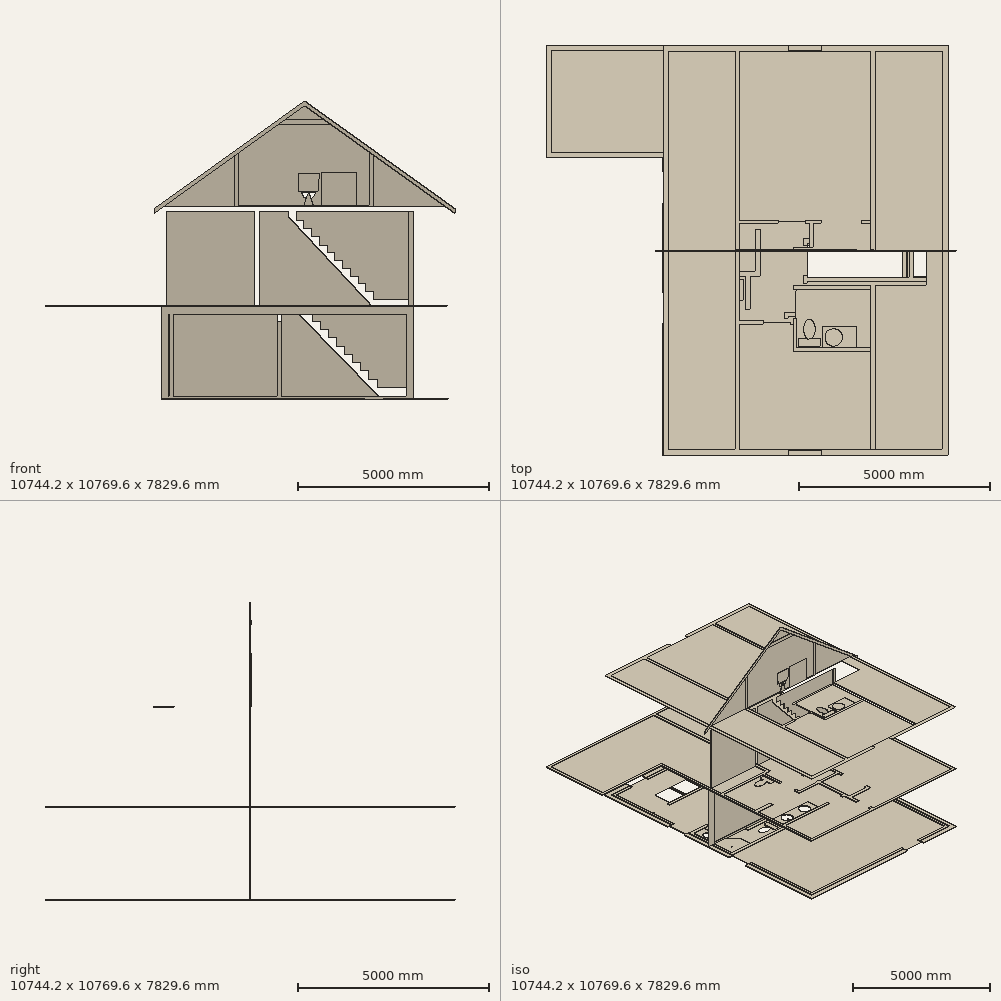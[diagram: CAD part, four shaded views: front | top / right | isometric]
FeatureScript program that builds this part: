
annotation { "Feature Type Name" : "Feature", "Feature Type Description" : "" }
export const myFeature = defineFeature(function(context is Context, id is Id, definition is map)
    precondition{}
    {
        {
            var Q0;
            Q0=qCreatedBy(makeId("Top.planeOp"),FACE);
            cPlane(context, id + "F0", {"entities" : qUnion([Q0]), "cplaneType" : CPlaneType.OFFSET, "offset" : 2438.4 * mm, "oppositeDirection" : true, "width" : 152.4 * mm, "height" : 152.4 * mm});
        }
        {
            var Q0;
            Q0=qCreatedBy(makeId("Top.planeOp"),FACE);
            cPlane(context, id + "F1", {"entities" : qUnion([Q0]), "cplaneType" : CPlaneType.OFFSET, "offset" : 2641.6 * mm, "width" : 152.4 * mm, "height" : 152.4 * mm});
        }
        {
            var Q0;
            Q0=qCreatedBy(id+"F0.planeOp",FACE);
            var sketch = newSketch(context, id + "F2", { "sketchPlane" : qUnion([Q0])});
            skLineSegment(sketch, "E0.bottom", {"start": v(-2901.95, -5207) * mm, "end": v(1898.65, -5207) * mm});
            skLineSegment(sketch, "E0.top", {"start": v(-2901.95, 5207) * mm, "end": v(3346.45, 5207) * mm});
            skLineSegment(sketch, "E0.left", {"start": v(-2901.95, -5207) * mm, "end": v(-2901.95, -1930.4) * mm});
            skLineSegment(sketch, "E0.right", {"start": v(4260.85, -5207) * mm, "end": v(4260.85, -863.6) * mm});
            skLineSegment(sketch, "E1.right", {"start": v(0, 5270.5) * mm, "end": v(0, -5207) * mm, "construction": true});
            skLineSegment(sketch, "E2", {"start": v(-2901.95, 0) * mm, "end": v(1722.7, 0) * mm, "construction": true});
            skLineSegment(sketch, "E3", {"start": v(463.55, -25.4) * mm, "end": v(463.55, -939.8) * mm});
            skLineSegment(sketch, "E4", {"start": v(463.55, -939.8) * mm, "end": v(666.75, -939.8) * mm});
            skLineSegment(sketch, "E5", {"start": v(666.75, -939.8) * mm, "end": v(666.75, -25.4) * mm});
            skLineSegment(sketch, "E6", {"start": v(666.75, -25.4) * mm, "end": v(869.95, -25.4) * mm});
            skLineSegment(sketch, "E7", {"start": v(869.95, -939.8) * mm, "end": v(869.95, -25.4) * mm});
            skLineSegment(sketch, "E8", {"start": v(463.55, -25.4) * mm, "end": v(666.75, -25.4) * mm});
            skLineSegment(sketch, "E9", {"start": v(666.75, -939.8) * mm, "end": v(869.95, -939.8) * mm});
            skLineSegment(sketch, "E10", {"start": v(869.95, -939.8) * mm, "end": v(1073.15, -939.8) * mm});
            skLineSegment(sketch, "E11", {"start": v(1073.15, -939.8) * mm, "end": v(1073.15, -25.4) * mm});
            skLineSegment(sketch, "E12", {"start": v(869.95, -25.4) * mm, "end": v(1073.15, -25.4) * mm});
            skLineSegment(sketch, "E13", {"start": v(1073.15, -25.4) * mm, "end": v(1276.35, -25.4) * mm});
            skLineSegment(sketch, "E14", {"start": v(1276.35, -939.8) * mm, "end": v(1276.35, -25.4) * mm});
            skLineSegment(sketch, "E15", {"start": v(1276.35, -939.8) * mm, "end": v(1073.15, -939.8) * mm});
            skLineSegment(sketch, "E16", {"start": v(1276.35, -25.4) * mm, "end": v(1479.55, -25.4) * mm});
            skLineSegment(sketch, "E17", {"start": v(1479.55, -25.4) * mm, "end": v(1479.55, -939.8) * mm});
            skLineSegment(sketch, "E18", {"start": v(1479.55, -939.8) * mm, "end": v(1276.35, -939.8) * mm});
            skLineSegment(sketch, "E19", {"start": v(1479.55, -25.4) * mm, "end": v(1682.75, -25.4) * mm});
            skLineSegment(sketch, "E20", {"start": v(1682.75, -25.4) * mm, "end": v(1682.75, -939.8) * mm});
            skLineSegment(sketch, "E21", {"start": v(1682.75, -939.8) * mm, "end": v(1479.55, -939.8) * mm});
            skLineSegment(sketch, "E22", {"start": v(1682.75, -25.4) * mm, "end": v(1885.95, -25.4) * mm});
            skLineSegment(sketch, "E23", {"start": v(1885.95, -25.4) * mm, "end": v(1885.95, -939.8) * mm});
            skLineSegment(sketch, "E24", {"start": v(1885.95, -939.8) * mm, "end": v(1682.75, -939.8) * mm});
            skLineSegment(sketch, "E25", {"start": v(1885.95, -25.4) * mm, "end": v(2089.15, -25.4) * mm});
            skLineSegment(sketch, "E26", {"start": v(2089.15, -25.4) * mm, "end": v(2089.15, -939.8) * mm});
            skLineSegment(sketch, "E27", {"start": v(2089.15, -939.8) * mm, "end": v(1885.95, -939.8) * mm});
            skLineSegment(sketch, "E28", {"start": v(2089.15, -25.4) * mm, "end": v(2292.35, -25.4) * mm});
            skLineSegment(sketch, "E29", {"start": v(2292.35, -25.4) * mm, "end": v(2292.35, -939.8) * mm});
            skLineSegment(sketch, "E30", {"start": v(2292.35, -939.8) * mm, "end": v(2089.15, -939.8) * mm});
            skLineSegment(sketch, "E31.bottom", {"start": v(-69.85, -1727.2) * mm, "end": v(69.85, -1727.2) * mm});
            skLineSegment(sketch, "E31.top", {"start": v(-69.85, -1879.6) * mm, "end": v(69.85, -1879.6) * mm});
            skLineSegment(sketch, "E31.left", {"start": v(-69.85, -1727.2) * mm, "end": v(-69.85, -1879.6) * mm});
            skLineSegment(sketch, "E31.right", {"start": v(69.85, -1727.2) * mm, "end": v(69.85, -1879.6) * mm});
            skLineSegment(sketch, "E32.bottom", {"start": v(69.85, 3175) * mm, "end": v(-69.85, 3175) * mm});
            skLineSegment(sketch, "E32.top", {"start": v(69.85, 3327.4) * mm, "end": v(-69.85, 3327.4) * mm});
            skLineSegment(sketch, "E32.left", {"start": v(69.85, 3175) * mm, "end": v(69.85, 3327.4) * mm});
            skLineSegment(sketch, "E32.right", {"start": v(-69.85, 3175) * mm, "end": v(-69.85, 3327.4) * mm});
            skLineSegment(sketch, "E33.0", {"start": v(4438.65, -5384.8) * mm, "end": v(4438.65, -685.8) * mm});
            skLineSegment(sketch, "E33.1", {"start": v(-3079.75, -5384.8) * mm, "end": v(4438.65, -5384.8) * mm});
            skLineSegment(sketch, "E33.2", {"start": v(-3079.75, -5384.8) * mm, "end": v(-3079.75, -1930.4) * mm});
            skLineSegment(sketch, "E33.3", {"start": v(-3079.75, 5384.8) * mm, "end": v(3524.25, 5384.8) * mm});
            skLineSegment(sketch, "E34", {"start": v(-3079.75, 2082.8) * mm, "end": v(-2901.95, 2082.8) * mm});
            skLineSegment(sketch, "E35", {"start": v(-3079.75, 1244.6) * mm, "end": v(-2901.95, 1244.6) * mm});
            skLineSegment(sketch, "E36", {"start": v(-2990.85, 2082.8) * mm, "end": v(-2482.7, 1416.2) * mm});
            skLineSegment(sketch, "E37", {"start": v(-2990.85, 2082.8) * mm, "end": v(-2990.85, 1244.6) * mm});
            skLineSegment(sketch, "E38", {"start": v(-2774.95, 1193.8) * mm, "end": v(-1962.15, 1193.8) * mm});
            skLineSegment(sketch, "E39", {"start": v(-2774.95, 1079.5) * mm, "end": v(-1962.15, 1079.5) * mm});
            skLineSegment(sketch, "E40", {"start": v(-2774.95, 1193.8) * mm, "end": v(-2774.95, 1079.5) * mm});
            skLineSegment(sketch, "E41", {"start": v(-1962.15, 1193.8) * mm, "end": v(-1962.15, 1079.5) * mm});
            skLineSegment(sketch, "E42", {"start": v(-1962.15, 1136.65) * mm, "end": v(-1250.95, 1136.65) * mm});
            skLineSegment(sketch, "E43", {"start": v(-1962.15, 1136.65) * mm, "end": v(-1324.41, 821.85) * mm});
            skLineSegment(sketch, "E44", {"start": v(-1250.95, 1193.8) * mm, "end": v(-1250.95, 1079.5) * mm});
            skLineSegment(sketch, "E45", {"start": v(-1250.95, 1193.8) * mm, "end": v(-768.35, 1193.8) * mm});
            skLineSegment(sketch, "E46", {"start": v(-1250.95, 1079.5) * mm, "end": v(-1149.35, 1079.5) * mm});
            skLineSegment(sketch, "E47", {"start": v(-1035.05, 1079.5) * mm, "end": v(-1035.05, -50.8) * mm});
            skLineSegment(sketch, "E48", {"start": v(-1149.35, 1079.5) * mm, "end": v(-1149.35, -165.1) * mm});
            skLineSegment(sketch, "E49", {"start": v(2241.55, -977.9) * mm, "end": v(-19.05, -977.9) * mm});
            skLineSegment(sketch, "E50", {"start": v(2241.55, -1066.8) * mm, "end": v(-19.05, -1066.8) * mm});
            skLineSegment(sketch, "E51.bottom", {"start": v(-251.05, -835.46) * mm, "end": v(-251.05, -276.66) * mm});
            skLineSegment(sketch, "E51.top", {"start": v(-454.25, -835.46) * mm, "end": v(-454.25, -276.66) * mm});
            skLineSegment(sketch, "E51.left", {"start": v(-454.25, -835.46) * mm, "end": v(-251.05, -835.46) * mm});
            skLineSegment(sketch, "E51.right", {"start": v(-454.25, -276.66) * mm, "end": v(-251.05, -276.66) * mm});
            skEllipse(sketch, "E52", {"center": v(-703.17, -556.06) * mm, "majorRadius": 259.08 * mm, "minorRadius": 152.4 * mm, "majorAxis": v(-1, 0)});
            skLineSegment(sketch, "E53", {"start": v(-454.25, -556.06) * mm, "end": v(-703.17, -556.06) * mm});
            skPoint(sketch, "E53.endSnap0", {"position": v(-962.25, -556.06) * mm});
            skLineSegment(sketch, "E54", {"start": v(206.15, -835.46) * mm, "end": v(-352.65, -835.46) * mm, "construction": true});
            skPoint(sketch, "E54.endSnap0", {"position": v(-352.65, -276.66) * mm});
            skLineSegment(sketch, "E55", {"start": v(-962.25, -556.06) * mm, "end": v(-330.86, -556.06) * mm});
            skLineSegment(sketch, "E56", {"start": v(-2876.55, -5181.6) * mm, "end": v(1898.65, -5181.6) * mm});
            skLineSegment(sketch, "E57", {"start": v(4235.45, -5181.6) * mm, "end": v(4235.45, -889) * mm});
            skLineSegment(sketch, "E58", {"start": v(4133.85, -990.6) * mm, "end": v(4133.85, -5080) * mm});
            skLineSegment(sketch, "E59", {"start": v(4133.85, -5080) * mm, "end": v(2736.85, -5080) * mm});
            skLineSegment(sketch, "E60", {"start": v(-2774.95, -5080) * mm, "end": v(-2774.95, -1930.4) * mm});
            skLineSegment(sketch, "E61", {"start": v(-2774.95, 1244.6) * mm, "end": v(-2876.55, 1244.6) * mm});
            skLineSegment(sketch, "E62", {"start": v(-2876.55, 1244.6) * mm, "end": v(-2876.55, -1092.2) * mm});
            skLineSegment(sketch, "E63", {"start": v(1898.65, -5080) * mm, "end": v(-2774.95, -5080) * mm});
            skLineSegment(sketch, "E64", {"start": v(4260.85, -863.6) * mm, "end": v(3346.45, -863.6) * mm});
            skLineSegment(sketch, "E65", {"start": v(3346.45, -863.6) * mm, "end": v(3346.45, 5207) * mm});
            skLineSegment(sketch, "E66", {"start": v(4438.65, -685.8) * mm, "end": v(3524.25, -685.8) * mm});
            skLineSegment(sketch, "E67", {"start": v(3524.25, -685.8) * mm, "end": v(3524.25, 5384.8) * mm});
            skLineSegment(sketch, "E68", {"start": v(3321.05, -889) * mm, "end": v(4235.45, -889) * mm});
            skLineSegment(sketch, "E69", {"start": v(4133.85, -990.6) * mm, "end": v(3219.45, -990.6) * mm});
            skLineSegment(sketch, "E70", {"start": v(3321.05, -889) * mm, "end": v(3321.05, 5181.6) * mm});
            skLineSegment(sketch, "E71", {"start": v(3219.45, -990.6) * mm, "end": v(3219.45, 5080) * mm});
            skLineSegment(sketch, "E72", {"start": v(3321.05, 5181.6) * mm, "end": v(-1098.55, 5181.6) * mm});
            skLineSegment(sketch, "E73", {"start": v(3219.45, 5080) * mm, "end": v(-1098.55, 5080) * mm});
            skLineSegment(sketch, "E74", {"start": v(-2876.55, 5181.6) * mm, "end": v(-2876.55, 2082.8) * mm});
            skLineSegment(sketch, "E75", {"start": v(-2774.95, 5080) * mm, "end": v(-2774.95, 2082.8) * mm});
            skLineSegment(sketch, "E76", {"start": v(-2876.55, 2082.8) * mm, "end": v(-2774.95, 2082.8) * mm});
            skLineSegment(sketch, "E77", {"start": v(-3079.75, -1092.2) * mm, "end": v(-2901.95, -1092.2) * mm});
            skLineSegment(sketch, "E78", {"start": v(-3079.75, -1930.4) * mm, "end": v(-2901.95, -1930.4) * mm});
            skLineSegment(sketch, "E79", {"start": v(-2990.85, -1092.2) * mm, "end": v(-2990.85, -1930.4) * mm});
            skLineSegment(sketch, "E80", {"start": v(-2876.55, -1092.2) * mm, "end": v(-2774.95, -1092.2) * mm});
            skLineSegment(sketch, "E81", {"start": v(-2876.55, -1930.4) * mm, "end": v(-2774.95, -1930.4) * mm});
            skLineSegment(sketch, "E82.trimOffspring", {"start": v(-2876.55, -1930.4) * mm, "end": v(-2876.55, -5181.6) * mm});
            skLineSegment(sketch, "E83.trimOffspring", {"start": v(-2774.95, -1092.2) * mm, "end": v(-2774.95, 1244.6) * mm});
            skLineSegment(sketch, "E84.trimOffspring", {"start": v(-2901.95, -1092.2) * mm, "end": v(-2901.95, 1244.6) * mm});
            skLineSegment(sketch, "E85.trimOffspring", {"start": v(-3079.75, -1092.2) * mm, "end": v(-3079.75, 1244.6) * mm});
            skLineSegment(sketch, "E86.trimOffspring", {"start": v(-3079.75, 2082.8) * mm, "end": v(-3079.75, 5384.8) * mm});
            skLineSegment(sketch, "E87.trimOffspring", {"start": v(-2901.95, 2082.8) * mm, "end": v(-2901.95, 5207) * mm});
            skLineSegment(sketch, "E88", {"start": v(-3079.75, -1092.2) * mm, "end": v(-3079.75, -1930.4) * mm});
            skLineSegment(sketch, "E89", {"start": v(-2901.95, -1092.2) * mm, "end": v(-2901.95, -1930.4) * mm});
            skLineSegment(sketch, "E90", {"start": v(-1936.75, 5384.8) * mm, "end": v(-1936.75, 5207) * mm});
            skLineSegment(sketch, "E91", {"start": v(-1098.55, 5384.8) * mm, "end": v(-1098.55, 5207) * mm});
            skLineSegment(sketch, "E92", {"start": v(-1936.75, 5295.9) * mm, "end": v(-1098.55, 5295.9) * mm});
            skLineSegment(sketch, "E93.trimOffspring", {"start": v(-1936.75, 5181.6) * mm, "end": v(-2876.55, 5181.6) * mm});
            skLineSegment(sketch, "E94.trimOffspring", {"start": v(-1936.75, 5080) * mm, "end": v(-2774.95, 5080) * mm});
            skLineSegment(sketch, "E95", {"start": v(-1936.75, 5181.6) * mm, "end": v(-1936.75, 5080) * mm});
            skLineSegment(sketch, "E96", {"start": v(-1098.55, 5181.6) * mm, "end": v(-1098.55, 5080) * mm});
            skLineSegment(sketch, "E97", {"start": v(-2774.95, -927.1) * mm, "end": v(-2774.95, -1066.8) * mm});
            skLineSegment(sketch, "E98", {"start": v(-2774.95, -927.1) * mm, "end": v(-133.35, -927.1) * mm});
            skLineSegment(sketch, "E99", {"start": v(-2774.95, -1066.8) * mm, "end": v(-19.05, -1066.8) * mm});
            skLineSegment(sketch, "E100.bottom", {"start": v(-1755.03, 3333.88) * mm, "end": v(-993.03, 3333.88) * mm});
            skLineSegment(sketch, "E100.top", {"start": v(-1755.03, 4095.88) * mm, "end": v(-993.03, 4095.88) * mm});
            skLineSegment(sketch, "E100.left", {"start": v(-1755.03, 3333.88) * mm, "end": v(-1755.03, 4095.88) * mm});
            skLineSegment(sketch, "E100.right", {"start": v(-993.03, 3333.88) * mm, "end": v(-993.03, 4095.88) * mm});
            skLineSegment(sketch, "E101.bottom", {"start": v(-908.34, 3329.81) * mm, "end": v(-146.34, 3329.81) * mm});
            skLineSegment(sketch, "E101.top", {"start": v(-908.34, 4091.81) * mm, "end": v(-146.34, 4091.81) * mm});
            skLineSegment(sketch, "E101.left", {"start": v(-908.34, 3329.81) * mm, "end": v(-908.34, 4091.81) * mm});
            skLineSegment(sketch, "E101.right", {"start": v(-146.34, 3329.81) * mm, "end": v(-146.34, 4091.81) * mm});
            skLineSegment(sketch, "E102.bottom", {"start": v(-2749.55, 139.7) * mm, "end": v(-2749.55, 1054.1) * mm});
            skLineSegment(sketch, "E102.top", {"start": v(-2216.15, 139.7) * mm, "end": v(-2216.15, 1054.1) * mm});
            skLineSegment(sketch, "E102.left", {"start": v(-2749.55, 139.7) * mm, "end": v(-2216.15, 139.7) * mm});
            skLineSegment(sketch, "E102.right", {"start": v(-2749.55, 1054.1) * mm, "end": v(-2216.15, 1054.1) * mm});
            skCircle(sketch, "E103", {"center": v(-2474.62, 596.9) * mm, "radius": 203.2 * mm});
            skLineSegment(sketch, "E104", {"start": v(-2474.62, 139.7) * mm, "end": v(-2474.62, 1054.1) * mm, "construction": true});
            skLineSegment(sketch, "E105", {"start": v(-1035.05, 1079.5) * mm, "end": v(-768.35, 1079.5) * mm});
            skLineSegment(sketch, "E106", {"start": v(-768.35, 1193.8) * mm, "end": v(-768.35, 1079.5) * mm});
            skLineSegment(sketch, "E107", {"start": v(-768.35, 1136.65) * mm, "end": v(-107.95, 1136.65) * mm});
            skLineSegment(sketch, "E108", {"start": v(-107.95, 1193.8) * mm, "end": v(-107.95, 1079.5) * mm});
            skLineSegment(sketch, "E109", {"start": v(-768.35, 1136.65) * mm, "end": v(-205.42, 1481.96) * mm});
            skLineSegment(sketch, "E110", {"start": v(-107.95, 1193.8) * mm, "end": v(298.45, 1193.8) * mm});
            skLineSegment(sketch, "E111", {"start": v(298.45, 1079.5) * mm, "end": v(298.45, 1193.8) * mm});
            skLineSegment(sketch, "E112", {"start": v(298.45, 1079.5) * mm, "end": v(-107.95, 1079.5) * mm});
            skLineSegment(sketch, "E113", {"start": v(1898.65, -5384.8) * mm, "end": v(1898.65, -5080) * mm});
            skLineSegment(sketch, "E114", {"start": v(2736.85, -5080) * mm, "end": v(2736.85, -5384.8) * mm});
            skLineSegment(sketch, "E115.trimOffspring", {"start": v(2736.85, -5181.6) * mm, "end": v(4235.45, -5181.6) * mm});
            skLineSegment(sketch, "E116.trimOffspring", {"start": v(2736.85, -5207) * mm, "end": v(4260.85, -5207) * mm});
            skLineSegment(sketch, "E117", {"start": v(1898.65, -5295.9) * mm, "end": v(2736.85, -5295.9) * mm});
            skLineSegment(sketch, "E118", {"start": v(2736.85, -5207) * mm, "end": v(2736.85, -5384.8) * mm});
            skLineSegment(sketch, "E119", {"start": v(1898.65, -5207) * mm, "end": v(1898.65, -5384.8) * mm});
            skLineSegment(sketch, "E120", {"start": v(184.15, 1079.5) * mm, "end": v(298.45, 1079.5) * mm});
            skLineSegment(sketch, "E121", {"start": v(298.45, 1079.5) * mm, "end": v(184.15, 1079.5) * mm});
            skLineSegment(sketch, "E122", {"start": v(184.15, 1079.5) * mm, "end": v(184.15, 12.7) * mm});
            skLineSegment(sketch, "E123", {"start": v(184.15, 12.7) * mm, "end": v(2241.55, 12.7) * mm});
            skLineSegment(sketch, "E124", {"start": v(2241.55, 12.7) * mm, "end": v(2241.55, 850.9) * mm});
            skLineSegment(sketch, "E125", {"start": v(1822.45, 850.9) * mm, "end": v(1822.45, 736.6) * mm});
            skLineSegment(sketch, "E126", {"start": v(1822.45, 736.6) * mm, "end": v(2127.25, 736.6) * mm});
            skLineSegment(sketch, "E127", {"start": v(2127.25, 736.6) * mm, "end": v(2127.25, 127) * mm});
            skLineSegment(sketch, "E128", {"start": v(2127.25, 127) * mm, "end": v(298.45, 127) * mm});
            skLineSegment(sketch, "E129", {"start": v(298.45, 127) * mm, "end": v(298.45, 1079.5) * mm});
            skLineSegment(sketch, "E130", {"start": v(-1149.35, -165.1) * mm, "end": v(-133.35, -165.1) * mm});
            skLineSegment(sketch, "E131", {"start": v(-133.35, -927.1) * mm, "end": v(-133.35, -165.1) * mm});
            skLineSegment(sketch, "E132", {"start": v(-1035.05, -50.8) * mm, "end": v(-19.05, -50.8) * mm});
            skLineSegment(sketch, "E133", {"start": v(-19.05, -50.8) * mm, "end": v(-19.05, -1066.8) * mm});
            skLineSegment(sketch, "E134", {"start": v(-19.05, -977.9) * mm, "end": v(-19.05, -1066.8) * mm});
            skLineSegment(sketch, "E135", {"start": v(-2770.45, -923.46) * mm, "end": v(-2770.45, 41.74) * mm});
            skLineSegment(sketch, "E136", {"start": v(-2770.45, 41.74) * mm, "end": v(-2262.45, 41.74) * mm});
            skLineSegment(sketch, "E137", {"start": v(-2262.45, 41.74) * mm, "end": v(-1803.35, -419.08) * mm});
            skLineSegment(sketch, "E138", {"start": v(-1803.35, -419.08) * mm, "end": v(-1805.26, -927.07) * mm});
            skLineSegment(sketch, "E139", {"start": v(-1805.26, -927.07) * mm, "end": v(-2770.45, -923.46) * mm});
            skLineSegment(sketch, "E140", {"start": v(-69.85, -927.1) * mm, "end": v(-69.85, -1079.5) * mm});
            skLineSegment(sketch, "E141", {"start": v(-69.85, -1079.5) * mm, "end": v(69.85, -1079.5) * mm});
            skLineSegment(sketch, "E142", {"start": v(69.85, -1079.5) * mm, "end": v(69.85, -927.1) * mm});
            skLineSegment(sketch, "E143", {"start": v(69.85, -927.1) * mm, "end": v(-69.85, -927.1) * mm});
            skLineSegment(sketch, "E144", {"start": v(-69.85, 1016) * mm, "end": v(69.85, 1016) * mm});
            skLineSegment(sketch, "E145", {"start": v(69.85, 1016) * mm, "end": v(69.85, 1168.4) * mm});
            skLineSegment(sketch, "E146", {"start": v(69.85, 1168.4) * mm, "end": v(-69.85, 1168.4) * mm});
            skLineSegment(sketch, "E147", {"start": v(-69.85, 1168.4) * mm, "end": v(-69.85, 1016) * mm});
            skLineSegment(sketch, "E148", {"start": v(3219.45, -25.4) * mm, "end": v(3219.45, -939.8) * mm});
            skLineSegment(sketch, "E149", {"start": v(3219.45, -939.8) * mm, "end": v(2495.55, -939.8) * mm});
            skLineSegment(sketch, "E150", {"start": v(2495.55, -939.8) * mm, "end": v(2495.55, -25.4) * mm});
            skLineSegment(sketch, "E151", {"start": v(2495.55, -25.4) * mm, "end": v(3219.45, -25.4) * mm});
            skLineSegment(sketch, "E152", {"start": v(2292.35, -25.4) * mm, "end": v(2495.55, -25.4) * mm});
            skLineSegment(sketch, "E153", {"start": v(2292.35, -939.8) * mm, "end": v(2495.55, -939.8) * mm});
            skLineSegment(sketch, "E154", {"start": v(-528.09, 989.03) * mm, "end": v(-70.89, 989.03) * mm});
            skLineSegment(sketch, "E155", {"start": v(-70.89, 989.03) * mm, "end": v(-70.89, 74.64) * mm});
            skLineSegment(sketch, "E156", {"start": v(-70.89, 74.64) * mm, "end": v(-533.4, 74.64) * mm});
            skLineSegment(sketch, "E157", {"start": v(-533.4, 74.64) * mm, "end": v(-528.09, 989.03) * mm});
            skLineSegment(sketch, "E158", {"start": v(2241.55, -977.9) * mm, "end": v(2241.55, -1066.8) * mm});
            skCircle(sketch, "E159", {"center": v(-2465.65, -619.8) * mm, "radius": 25.37 * mm});
            skLineSegment(sketch, "E160", {"start": v(-2774.95, 3289.3) * mm, "end": v(-2774.95, 3175) * mm});
            skLineSegment(sketch, "E161", {"start": v(-2774.95, 3175) * mm, "end": v(-2698.75, 3175) * mm});
            skLineSegment(sketch, "E162", {"start": v(-2698.75, 3175) * mm, "end": v(-2698.75, 3289.3) * mm});
            skLineSegment(sketch, "E163", {"start": v(-2698.75, 3289.3) * mm, "end": v(-2774.95, 3289.3) * mm});
            skLineSegment(sketch, "E164", {"start": v(-2698.75, 3232.15) * mm, "end": v(-1885.95, 3232.15) * mm});
            skLineSegment(sketch, "E165", {"start": v(-1885.95, 3289.3) * mm, "end": v(-1885.95, 3175) * mm});
            skLineSegment(sketch, "E166", {"start": v(-1885.95, 3175) * mm, "end": v(69.85, 3175) * mm});
            skLineSegment(sketch, "E167", {"start": v(-69.85, 5080) * mm, "end": v(-69.85, 3289.3) * mm});
            skLineSegment(sketch, "E168", {"start": v(-69.85, 3289.3) * mm, "end": v(-1885.95, 3289.3) * mm});
            skLineSegment(sketch, "E169", {"start": v(-69.85, 5080) * mm, "end": v(69.85, 5080) * mm});
            skLineSegment(sketch, "E170", {"start": v(69.85, 5080) * mm, "end": v(69.85, 3175) * mm});
            skLineSegment(sketch, "E171", {"start": v(-2698.75, 3232.15) * mm, "end": v(-1944.43, 3534.9) * mm});
            skLineSegment(sketch, "E172", {"start": v(298.45, 850.9) * mm, "end": v(298.45, 736.6) * mm});
            skLineSegment(sketch, "E173", {"start": v(298.45, 736.6) * mm, "end": v(603.25, 736.6) * mm});
            skLineSegment(sketch, "E174", {"start": v(603.25, 736.6) * mm, "end": v(603.25, 850.9) * mm});
            skLineSegment(sketch, "E175", {"start": v(603.25, 850.9) * mm, "end": v(298.45, 850.9) * mm});
            skLineSegment(sketch, "E176", {"start": v(1822.45, 850.9) * mm, "end": v(2241.55, 850.9) * mm});
            skCircle(sketch, "E177", {"center": v(264.69, -453.92) * mm, "radius": 228.6 * mm});
            skSolve(sketch);
        }
        {
            var Q0;
            Q0=qCreatedBy(id+"F1.planeOp",FACE);
            var sketch = newSketch(context, id + "F3", { "sketchPlane" : qUnion([Q0])});
            skLineSegment(sketch, "E178.bottom", {"start": v(-2914.65, -5219.7) * mm, "end": v(4273.55, -5219.7) * mm});
            skLineSegment(sketch, "E178.top", {"start": v(-2914.65, 5219.7) * mm, "end": v(4273.55, 5219.7) * mm});
            skLineSegment(sketch, "E178.left", {"start": v(-2914.65, -5219.7) * mm, "end": v(-2914.65, 5219.7) * mm});
            skLineSegment(sketch, "E178.right", {"start": v(4273.55, -5219.7) * mm, "end": v(4273.55, 5219.7) * mm});
            skLineSegment(sketch, "E179", {"start": v(-3657.6, 0) * mm, "end": v(4273.55, 0) * mm, "construction": true});
            skLineSegment(sketch, "E180", {"start": v(0, 5257.8) * mm, "end": v(0, -5257.8) * mm, "construction": true});
            skLineSegment(sketch, "E181.0", {"start": v(4425.95, -5372.1) * mm, "end": v(4425.95, 5372.1) * mm});
            skLineSegment(sketch, "E181.1", {"start": v(-3067.05, -5372.1) * mm, "end": v(4425.95, -5372.1) * mm});
            skLineSegment(sketch, "E181.2", {"start": v(-3067.05, -5372.1) * mm, "end": v(-3067.05, 5372.1) * mm});
            skLineSegment(sketch, "E181.3", {"start": v(-3067.05, 5372.1) * mm, "end": v(4425.95, 5372.1) * mm});
            skLineSegment(sketch, "E182", {"start": v(2381.25, 5219.7) * mm, "end": v(2381.25, -5219.7) * mm});
            skLineSegment(sketch, "E183", {"start": v(-1047.75, 5219.7) * mm, "end": v(-1047.75, -5219.7) * mm});
            skLineSegment(sketch, "E184.0", {"start": v(2508.25, 5219.7) * mm, "end": v(2508.25, -5219.7) * mm});
            skLineSegment(sketch, "E185.0", {"start": v(-1174.75, 5219.7) * mm, "end": v(-1174.75, -5219.7) * mm});
            skLineSegment(sketch, "E186.left", {"start": v(3079.75, -12.7) * mm, "end": v(3079.75, -927.1) * mm});
            skLineSegment(sketch, "E187", {"start": v(2851.15, -12.7) * mm, "end": v(2851.15, -927.1) * mm});
            skLineSegment(sketch, "E188", {"start": v(2622.55, -12.7) * mm, "end": v(2622.55, -927.1) * mm});
            skLineSegment(sketch, "E189", {"start": v(2393.95, -927.1) * mm, "end": v(2393.95, -12.7) * mm});
            skLineSegment(sketch, "E190", {"start": v(2393.95, -12.7) * mm, "end": v(2165.35, -12.7) * mm});
            skLineSegment(sketch, "E191", {"start": v(2165.35, -12.7) * mm, "end": v(2165.35, -927.1) * mm});
            skLineSegment(sketch, "E192", {"start": v(1936.75, -927.1) * mm, "end": v(1936.75, -12.7) * mm});
            skLineSegment(sketch, "E193", {"start": v(1936.75, -12.7) * mm, "end": v(1708.15, -12.7) * mm});
            skLineSegment(sketch, "E194", {"start": v(1708.15, -12.7) * mm, "end": v(1708.15, -927.1) * mm});
            skLineSegment(sketch, "E195", {"start": v(1479.55, -927.1) * mm, "end": v(1479.55, -12.7) * mm});
            skLineSegment(sketch, "E196", {"start": v(1479.55, -12.7) * mm, "end": v(1250.95, -12.7) * mm});
            skLineSegment(sketch, "E197", {"start": v(1250.95, -12.7) * mm, "end": v(1250.95, -927.1) * mm});
            skLineSegment(sketch, "E198", {"start": v(1022.35, -927.1) * mm, "end": v(1022.35, -12.7) * mm});
            skLineSegment(sketch, "E199", {"start": v(2851.15, -12.7) * mm, "end": v(3079.75, -12.7) * mm});
            skLineSegment(sketch, "E200", {"start": v(1022.35, -12.7) * mm, "end": v(793.75, -12.7) * mm});
            skLineSegment(sketch, "E201", {"start": v(793.75, -12.7) * mm, "end": v(793.75, -927.1) * mm});
            skLineSegment(sketch, "E202", {"start": v(565.15, -927.1) * mm, "end": v(565.15, -12.7) * mm});
            skLineSegment(sketch, "E203", {"start": v(565.15, -12.7) * mm, "end": v(336.55, -12.7) * mm});
            skLineSegment(sketch, "E204", {"start": v(336.55, -12.7) * mm, "end": v(336.55, -927.1) * mm});
            skLineSegment(sketch, "E205", {"start": v(1098.55, 5219.7) * mm, "end": v(1098.55, 5372.1) * mm});
            skLineSegment(sketch, "E206", {"start": v(234.95, 5219.7) * mm, "end": v(234.95, 5372.1) * mm});
            skLineSegment(sketch, "E207", {"start": v(1098.55, 5295.9) * mm, "end": v(234.95, 5295.9) * mm});
            skLineSegment(sketch, "E208", {"start": v(666.75, 4864.1) * mm, "end": v(666.75, 5295.9) * mm, "construction": true});
            skLineSegment(sketch, "E209", {"start": v(1098.55, -5219.7) * mm, "end": v(1098.55, -5372.1) * mm});
            skLineSegment(sketch, "E210", {"start": v(1098.55, -5372.1) * mm, "end": v(1098.55, -5295.9) * mm});
            skLineSegment(sketch, "E211", {"start": v(1098.55, -5295.9) * mm, "end": v(234.95, -5295.9) * mm});
            skLineSegment(sketch, "E212", {"start": v(234.95, -5219.7) * mm, "end": v(234.95, -5372.1) * mm});
            skLineSegment(sketch, "E213", {"start": v(666.75, -5295.9) * mm, "end": v(666.75, -5575.3) * mm, "construction": true});
            skLineSegment(sketch, "E214", {"start": v(-31.75, 800.1) * mm, "end": v(-31.75, 698.5) * mm});
            skLineSegment(sketch, "E215", {"start": v(679.45, 800.1) * mm, "end": v(679.45, 698.5) * mm});
            skLineSegment(sketch, "E216", {"start": v(-1047.75, 698.5) * mm, "end": v(-31.75, 698.5) * mm});
            skLineSegment(sketch, "E217", {"start": v(-1047.75, 800.1) * mm, "end": v(-31.75, 800.1) * mm});
            skLineSegment(sketch, "E218", {"start": v(3841.75, -12.7) * mm, "end": v(3079.75, -12.7) * mm});
            skLineSegment(sketch, "E219", {"start": v(3841.75, -927.1) * mm, "end": v(3079.75, -927.1) * mm});
            skLineSegment(sketch, "E220", {"start": v(565.15, -12.7) * mm, "end": v(793.75, -12.7) * mm});
            skLineSegment(sketch, "E221", {"start": v(1022.35, -12.7) * mm, "end": v(1250.95, -12.7) * mm});
            skLineSegment(sketch, "E222", {"start": v(1479.55, -12.7) * mm, "end": v(1708.15, -12.7) * mm});
            skLineSegment(sketch, "E223", {"start": v(1936.75, -12.7) * mm, "end": v(2165.35, -12.7) * mm});
            skLineSegment(sketch, "E224", {"start": v(2393.95, -12.7) * mm, "end": v(2622.55, -12.7) * mm});
            skLineSegment(sketch, "E225", {"start": v(2622.55, -12.7) * mm, "end": v(2851.15, -12.7) * mm});
            skLineSegment(sketch, "E226", {"start": v(3079.75, -927.1) * mm, "end": v(336.55, -927.1) * mm});
            skLineSegment(sketch, "E227", {"start": v(-31.75, 749.3) * mm, "end": v(679.45, 749.3) * mm});
            skLineSegment(sketch, "E228", {"start": v(42.68, 1066.05) * mm, "end": v(679.45, 749.3) * mm});
            skLineSegment(sketch, "E229", {"start": v(679.45, 800.1) * mm, "end": v(1085.85, 800.1) * mm});
            skLineSegment(sketch, "E230", {"start": v(1085.85, 800.1) * mm, "end": v(1085.85, 698.5) * mm});
            skLineSegment(sketch, "E231", {"start": v(882.65, 88.9) * mm, "end": v(781.05, 88.9) * mm});
            skLineSegment(sketch, "E232", {"start": v(781.05, 88.9) * mm, "end": v(781.05, 698.5) * mm});
            skLineSegment(sketch, "E233", {"start": v(1085.85, 698.5) * mm, "end": v(679.45, 698.5) * mm});
            skLineSegment(sketch, "E234", {"start": v(450.85, -2552.7) * mm, "end": v(2381.25, -2552.7) * mm});
            skLineSegment(sketch, "E235", {"start": v(450.85, -2552.7) * mm, "end": v(450.85, -2654.3) * mm});
            skLineSegment(sketch, "E236", {"start": v(2381.25, -2654.3) * mm, "end": v(450.85, -2654.3) * mm});
            skLineSegment(sketch, "E237.bottom", {"start": v(1111.25, -2006.6) * mm, "end": v(2025.65, -2006.6) * mm});
            skLineSegment(sketch, "E237.top", {"start": v(1111.25, -2540) * mm, "end": v(2025.65, -2540) * mm});
            skLineSegment(sketch, "E237.left", {"start": v(1111.25, -2006.6) * mm, "end": v(1111.25, -2540) * mm});
            skLineSegment(sketch, "E237.right", {"start": v(2025.65, -2006.6) * mm, "end": v(2025.65, -2540) * mm});
            skCircle(sketch, "E238", {"center": v(1416.05, -2286) * mm, "radius": 228.6 * mm});
            skLineSegment(sketch, "E239.bottom", {"start": v(349.25, -1028.7) * mm, "end": v(2381.25, -1028.7) * mm});
            skLineSegment(sketch, "E239.top", {"start": v(349.25, -927.1) * mm, "end": v(2381.25, -927.1) * mm});
            skLineSegment(sketch, "E239.right", {"start": v(2381.25, -927.1) * mm, "end": v(2381.25, -1028.7) * mm});
            skLineSegment(sketch, "E240", {"start": v(349.25, -927.1) * mm, "end": v(349.25, -1028.7) * mm});
            skLineSegment(sketch, "E241.bottom", {"start": v(501.65, -2527.3) * mm, "end": v(1060.45, -2527.3) * mm});
            skLineSegment(sketch, "E241.top", {"start": v(501.65, -2324.1) * mm, "end": v(1060.45, -2324.1) * mm});
            skLineSegment(sketch, "E241.left", {"start": v(501.65, -2324.1) * mm, "end": v(501.65, -2527.3) * mm});
            skLineSegment(sketch, "E241.right", {"start": v(1060.45, -2324.1) * mm, "end": v(1060.45, -2527.3) * mm});
            skEllipse(sketch, "E242", {"center": v(781.05, -2075.18) * mm, "majorRadius": 259.08 * mm, "minorRadius": 152.4 * mm, "majorAxis": v(0, 1)});
            skLineSegment(sketch, "E243", {"start": v(781.05, -2324.1) * mm, "end": v(781.05, -2075.18) * mm});
            skPoint(sketch, "E243.endSnap0", {"position": v(781.05, -1816.1) * mm});
            skLineSegment(sketch, "E244", {"start": v(1060.45, -2425.7) * mm, "end": v(501.65, -2425.7) * mm, "construction": true});
            skPoint(sketch, "E244.endSnap0", {"position": v(1060.45, -2425.7) * mm});
            skLineSegment(sketch, "E245", {"start": v(781.05, -1816.1) * mm, "end": v(781.05, -2334.26) * mm});
            skLineSegment(sketch, "E246", {"start": v(349.25, -12.7) * mm, "end": v(2381.25, -12.7) * mm});
            skLineSegment(sketch, "E247", {"start": v(349.25, -12.7) * mm, "end": v(349.25, 88.9) * mm});
            skLineSegment(sketch, "E248", {"start": v(2381.25, 698.5) * mm, "end": v(2381.25, 800.1) * mm});
            skLineSegment(sketch, "E249", {"start": v(2381.25, 800.1) * mm, "end": v(2152.65, 800.1) * mm});
            skLineSegment(sketch, "E250", {"start": v(2152.65, 800.1) * mm, "end": v(2152.65, 698.5) * mm});
            skLineSegment(sketch, "E251", {"start": v(2152.65, 698.5) * mm, "end": v(2381.25, 698.5) * mm});
            skLineSegment(sketch, "E252", {"start": v(2381.25, -12.7) * mm, "end": v(2381.25, 88.9) * mm});
            skLineSegment(sketch, "E253", {"start": v(2381.25, 88.9) * mm, "end": v(349.25, 88.9) * mm});
            skLineSegment(sketch, "E254", {"start": v(781.05, 698.5) * mm, "end": v(882.65, 698.5) * mm});
            skLineSegment(sketch, "E255", {"start": v(882.65, 698.5) * mm, "end": v(882.65, 88.9) * mm});
            skLineSegment(sketch, "E256", {"start": v(349.25, -1028.7) * mm, "end": v(450.85, -1028.7) * mm});
            skLineSegment(sketch, "E257", {"start": v(450.85, -1028.7) * mm, "end": v(450.85, -1079.5) * mm});
            skLineSegment(sketch, "E258", {"start": v(450.85, -1079.5) * mm, "end": v(349.25, -1079.5) * mm});
            skLineSegment(sketch, "E259", {"start": v(349.25, -1079.5) * mm, "end": v(349.25, -1028.7) * mm});
            skLineSegment(sketch, "E260", {"start": v(400.05, -1079.5) * mm, "end": v(400.05, -1790.7) * mm});
            skLineSegment(sketch, "E261", {"start": v(400.05, -1079.5) * mm, "end": v(650.16, -1745.27) * mm});
            skLineSegment(sketch, "E262", {"start": v(349.25, -1790.7) * mm, "end": v(450.85, -1790.7) * mm});
            skLineSegment(sketch, "E263", {"start": v(450.85, -1790.7) * mm, "end": v(450.85, -2654.3) * mm});
            skLineSegment(sketch, "E264", {"start": v(450.85, -2654.3) * mm, "end": v(349.25, -2654.3) * mm});
            skLineSegment(sketch, "E265", {"start": v(349.25, -2654.3) * mm, "end": v(349.25, -1790.7) * mm});
            skLineSegment(sketch, "E266", {"start": v(349.25, -1829.9) * mm, "end": v(349.25, -1931.5) * mm});
            skLineSegment(sketch, "E267", {"start": v(349.25, -1931.5) * mm, "end": v(273.05, -1931.5) * mm});
            skLineSegment(sketch, "E268", {"start": v(273.05, -1931.5) * mm, "end": v(273.05, -1829.9) * mm});
            skLineSegment(sketch, "E269", {"start": v(273.05, -1829.9) * mm, "end": v(349.25, -1829.9) * mm});
            skLineSegment(sketch, "E270", {"start": v(273.05, -1880.7) * mm, "end": v(-438.15, -1880.7) * mm});
            skPoint(sketch, "E270.endSnap0", {"position": v(273.05, -1880.7) * mm});
            skLineSegment(sketch, "E271", {"start": v(-438.15, -1829.9) * mm, "end": v(-438.15, -1931.5) * mm});
            skLineSegment(sketch, "E272", {"start": v(273.05, -1880.7) * mm, "end": v(-313.04, -2283.57) * mm});
            skLineSegment(sketch, "E273", {"start": v(-438.15, -1829.9) * mm, "end": v(-1047.75, -1829.9) * mm});
            skLineSegment(sketch, "E274", {"start": v(-1047.75, -1829.9) * mm, "end": v(-1047.75, -1931.5) * mm});
            skLineSegment(sketch, "E275", {"start": v(-1047.75, -1931.5) * mm, "end": v(-438.15, -1931.5) * mm});
            skLineSegment(sketch, "E276", {"start": v(-1174.75, 5219.7) * mm, "end": v(-1047.75, 5219.7) * mm});
            skLineSegment(sketch, "E277", {"start": v(2508.25, 5219.7) * mm, "end": v(2381.25, 5219.7) * mm});
            skLineSegment(sketch, "E278", {"start": v(3841.75, -12.7) * mm, "end": v(3841.75, -927.1) * mm});
            skSolve(sketch);
        }
        {
            var Q0;
            Q0=qCreatedBy(makeId("Top.planeOp"),FACE);
            var sketch = newSketch(context, id + "F4", { "sketchPlane" : qUnion([Q0])});
            skLineSegment(sketch, "E279", {"start": v(-6115.05, 5372.1) * mm, "end": v(3511.55, 5372.1) * mm});
            skLineSegment(sketch, "E280", {"start": v(3511.55, 5372.1) * mm, "end": v(3511.55, 4660.9) * mm});
            skLineSegment(sketch, "E281", {"start": v(3511.55, 4660.9) * mm, "end": v(3892.55, 4660.9) * mm});
            skLineSegment(sketch, "E282", {"start": v(3892.55, 4660.9) * mm, "end": v(3892.55, 2197.1) * mm});
            skLineSegment(sketch, "E283", {"start": v(3892.55, 2197.1) * mm, "end": v(3511.55, 2197.1) * mm});
            skLineSegment(sketch, "E284", {"start": v(3511.55, 2197.1) * mm, "end": v(3511.55, -698.5) * mm});
            skLineSegment(sketch, "E285", {"start": v(3511.55, -698.5) * mm, "end": v(4425.95, -698.5) * mm});
            skLineSegment(sketch, "E286", {"start": v(4425.95, -698.5) * mm, "end": v(4425.95, -5372.1) * mm});
            skLineSegment(sketch, "E287", {"start": v(4425.95, -5372.1) * mm, "end": v(-3067.05, -5372.1) * mm});
            skLineSegment(sketch, "E288", {"start": v(-3067.05, -5372.1) * mm, "end": v(-3067.05, 2451.1) * mm});
            skLineSegment(sketch, "E289", {"start": v(-3067.05, 2451.1) * mm, "end": v(-6115.05, 2451.1) * mm});
            skLineSegment(sketch, "E290", {"start": v(-6115.05, 2451.1) * mm, "end": v(-6115.05, 5372.1) * mm});
            skLineSegment(sketch, "E291", {"start": v(-628.65, 5257.8) * mm, "end": v(-628.65, 1333.5) * mm});
            skLineSegment(sketch, "E292", {"start": v(-628.65, 1333.5) * mm, "end": v(-514.35, 1333.5) * mm});
            skLineSegment(sketch, "E293", {"start": v(-514.35, 1333.5) * mm, "end": v(-514.35, 5257.8) * mm});
            skLineSegment(sketch, "E294", {"start": v(-628.65, 5257.8) * mm, "end": v(-6000.75, 5257.8) * mm});
            skLineSegment(sketch, "E295", {"start": v(-6000.75, 5257.8) * mm, "end": v(-6000.75, 2565.4) * mm});
            skLineSegment(sketch, "E296", {"start": v(-6000.75, 2565.4) * mm, "end": v(-2952.75, 2565.4) * mm});
            skLineSegment(sketch, "E297", {"start": v(-2952.75, 2565.4) * mm, "end": v(-2952.75, -558.8) * mm});
            skLineSegment(sketch, "E298", {"start": v(-2952.75, -558.8) * mm, "end": v(-628.65, -558.8) * mm});
            skLineSegment(sketch, "E299", {"start": v(-628.65, -558.8) * mm, "end": v(-628.65, 558.8) * mm});
            skLineSegment(sketch, "E300", {"start": v(-628.65, 558.8) * mm, "end": v(-514.35, 558.8) * mm});
            skLineSegment(sketch, "E301", {"start": v(-514.35, 558.8) * mm, "end": v(-514.35, -673.1) * mm});
            skLineSegment(sketch, "E302", {"start": v(-514.35, -673.1) * mm, "end": v(-781.05, -673.1) * mm});
            skLineSegment(sketch, "E303", {"start": v(-781.05, -673.1) * mm, "end": v(-781.05, -1562.1) * mm});
            skLineSegment(sketch, "E304", {"start": v(-781.05, -2451.1) * mm, "end": v(120.65, -2451.1) * mm});
            skLineSegment(sketch, "E305", {"start": v(120.65, -2565.4) * mm, "end": v(-895.35, -2565.4) * mm});
            skLineSegment(sketch, "E306", {"start": v(-895.35, -1562.1) * mm, "end": v(-895.35, -673.1) * mm});
            skLineSegment(sketch, "E307", {"start": v(-895.35, -673.1) * mm, "end": v(-2952.75, -673.1) * mm});
            skLineSegment(sketch, "E308", {"start": v(-2952.75, -673.1) * mm, "end": v(-2952.75, -2324.1) * mm});
            skLineSegment(sketch, "E309", {"start": v(-2952.75, -2324.1) * mm, "end": v(-2190.75, -2324.1) * mm});
            skLineSegment(sketch, "E310", {"start": v(-2190.75, -2324.1) * mm, "end": v(-2190.75, -2476.5) * mm});
            skLineSegment(sketch, "E311", {"start": v(-2190.75, -2476.5) * mm, "end": v(-2952.75, -2476.5) * mm});
            skLineSegment(sketch, "E312", {"start": v(-2952.75, -2476.5) * mm, "end": v(-2952.75, -3771.9) * mm});
            skLineSegment(sketch, "E313", {"start": v(-2952.75, -3771.9) * mm, "end": v(-666.75, -3771.9) * mm});
            skLineSegment(sketch, "E314", {"start": v(120.65, -3771.9) * mm, "end": v(120.65, -2565.4) * mm});
            skLineSegment(sketch, "E315", {"start": v(120.65, -2451.1) * mm, "end": v(120.65, -2400.3) * mm});
            skLineSegment(sketch, "E316", {"start": v(120.65, -2400.3) * mm, "end": v(234.95, -2400.3) * mm});
            skLineSegment(sketch, "E317", {"start": v(234.95, -2400.3) * mm, "end": v(234.95, -2451.1) * mm});
            skLineSegment(sketch, "E318", {"start": v(234.95, -2451.1) * mm, "end": v(1123.95, -2451.1) * mm});
            skLineSegment(sketch, "E319", {"start": v(1123.95, -2451.1) * mm, "end": v(1123.95, -1739.9) * mm});
            skLineSegment(sketch, "E320", {"start": v(1123.95, -1739.9) * mm, "end": v(234.95, -1739.9) * mm});
            skLineSegment(sketch, "E321", {"start": v(234.95, -1739.9) * mm, "end": v(234.95, -1790.7) * mm});
            skLineSegment(sketch, "E322", {"start": v(234.95, -1790.7) * mm, "end": v(120.65, -1790.7) * mm});
            skLineSegment(sketch, "E323", {"start": v(120.65, -1790.7) * mm, "end": v(120.65, -1625.6) * mm});
            skLineSegment(sketch, "E324", {"start": v(120.65, -1625.6) * mm, "end": v(610.92, -1625.6) * mm});
            skLineSegment(sketch, "E325", {"start": v(610.92, -1625.6) * mm, "end": v(610.92, -1574.8) * mm});
            skLineSegment(sketch, "E326", {"start": v(610.92, -1574.8) * mm, "end": v(725.22, -1574.8) * mm});
            skLineSegment(sketch, "E327", {"start": v(725.22, -1574.8) * mm, "end": v(725.22, -1625.6) * mm});
            skLineSegment(sketch, "E328", {"start": v(725.22, -1625.6) * mm, "end": v(1238.25, -1625.6) * mm});
            skLineSegment(sketch, "E329", {"start": v(1238.25, -1625.6) * mm, "end": v(1238.25, -2717.8) * mm});
            skLineSegment(sketch, "E330", {"start": v(1238.25, -2717.8) * mm, "end": v(1123.95, -2717.8) * mm});
            skLineSegment(sketch, "E331", {"start": v(1123.95, -2717.8) * mm, "end": v(1123.95, -2565.4) * mm});
            skLineSegment(sketch, "E332", {"start": v(1123.95, -2565.4) * mm, "end": v(234.95, -2565.4) * mm});
            skLineSegment(sketch, "E333", {"start": v(234.95, -2565.4) * mm, "end": v(234.95, -4025.9) * mm});
            skLineSegment(sketch, "E334", {"start": v(234.95, -4025.9) * mm, "end": v(1123.95, -4025.9) * mm});
            skLineSegment(sketch, "E335", {"start": v(1123.95, -4025.9) * mm, "end": v(1123.95, -3937) * mm});
            skLineSegment(sketch, "E336", {"start": v(1123.95, -3937) * mm, "end": v(1238.25, -3937) * mm});
            skLineSegment(sketch, "E337", {"start": v(1238.25, -3937) * mm, "end": v(1238.25, -4140.2) * mm});
            skLineSegment(sketch, "E338", {"start": v(1238.25, -4140.2) * mm, "end": v(234.95, -4140.2) * mm});
            skLineSegment(sketch, "E339", {"start": v(234.95, -4140.2) * mm, "end": v(234.95, -4521.2) * mm});
            skLineSegment(sketch, "E340", {"start": v(234.95, -4521.2) * mm, "end": v(120.65, -4521.2) * mm});
            skLineSegment(sketch, "E341", {"start": v(120.65, -4521.2) * mm, "end": v(120.65, -3886.2) * mm});
            skLineSegment(sketch, "E342", {"start": v(-666.75, -3886.2) * mm, "end": v(-2952.75, -3886.2) * mm});
            skLineSegment(sketch, "E343", {"start": v(-2952.75, -3886.2) * mm, "end": v(-2952.75, -5257.8) * mm});
            skLineSegment(sketch, "E344", {"start": v(-2952.75, -5257.8) * mm, "end": v(120.65, -5257.8) * mm});
            skLineSegment(sketch, "E345", {"start": v(120.65, -5257.8) * mm, "end": v(120.65, -5130.8) * mm});
            skLineSegment(sketch, "E346", {"start": v(120.65, -5130.8) * mm, "end": v(234.95, -5130.8) * mm});
            skLineSegment(sketch, "E347", {"start": v(234.95, -5130.8) * mm, "end": v(234.95, -5257.8) * mm});
            skLineSegment(sketch, "E348", {"start": v(234.95, -5257.8) * mm, "end": v(4311.65, -5257.8) * mm});
            skLineSegment(sketch, "E349", {"start": v(4311.65, -5257.8) * mm, "end": v(4311.65, -812.8) * mm});
            skLineSegment(sketch, "E350", {"start": v(4311.65, -812.8) * mm, "end": v(725.22, -812.8) * mm});
            skLineSegment(sketch, "E351", {"start": v(725.22, -812.8) * mm, "end": v(725.22, -863.6) * mm});
            skLineSegment(sketch, "E352", {"start": v(725.22, -863.6) * mm, "end": v(610.92, -863.6) * mm});
            skLineSegment(sketch, "E353", {"start": v(610.92, -863.6) * mm, "end": v(610.92, -647.7) * mm});
            skLineSegment(sketch, "E354", {"start": v(610.92, -647.7) * mm, "end": v(725.22, -647.7) * mm});
            skLineSegment(sketch, "E355", {"start": v(725.22, -647.7) * mm, "end": v(725.22, -698.5) * mm});
            skLineSegment(sketch, "E356", {"start": v(725.22, -698.5) * mm, "end": v(3397.25, -698.5) * mm});
            skLineSegment(sketch, "E357", {"start": v(3397.25, -698.5) * mm, "end": v(3397.25, 190.5) * mm});
            skLineSegment(sketch, "E358", {"start": v(2584.45, 190.5) * mm, "end": v(725.22, 190.5) * mm});
            skLineSegment(sketch, "E359", {"start": v(725.22, 190.5) * mm, "end": v(725.22, 139.7) * mm});
            skLineSegment(sketch, "E360", {"start": v(725.22, 139.7) * mm, "end": v(610.92, 139.7) * mm});
            skLineSegment(sketch, "E361", {"start": v(610.92, 139.7) * mm, "end": v(610.92, 304.8) * mm});
            skLineSegment(sketch, "E362", {"start": v(610.92, 304.8) * mm, "end": v(2584.45, 304.8) * mm});
            skLineSegment(sketch, "E363", {"start": v(3397.25, 304.8) * mm, "end": v(3397.25, 2311.4) * mm});
            skLineSegment(sketch, "E364", {"start": v(3397.25, 2311.4) * mm, "end": v(3778.25, 2311.4) * mm});
            skLineSegment(sketch, "E365", {"start": v(3778.25, 2311.4) * mm, "end": v(3778.25, 4546.6) * mm});
            skLineSegment(sketch, "E366", {"start": v(3778.25, 4546.6) * mm, "end": v(3397.25, 4546.6) * mm});
            skLineSegment(sketch, "E367", {"start": v(3397.25, 4546.6) * mm, "end": v(3397.25, 5257.8) * mm});
            skLineSegment(sketch, "E368", {"start": v(3397.25, 5257.8) * mm, "end": v(-514.35, 5257.8) * mm});
            skLineSegment(sketch, "E369.bottom", {"start": v(-2947.9, -3233.86) * mm, "end": v(-2033.5, -3233.86) * mm});
            skLineSegment(sketch, "E369.top", {"start": v(-2947.9, -3767.26) * mm, "end": v(-2033.5, -3767.26) * mm});
            skLineSegment(sketch, "E369.left", {"start": v(-2947.9, -3233.86) * mm, "end": v(-2947.9, -3767.26) * mm});
            skLineSegment(sketch, "E369.right", {"start": v(-2033.5, -3233.86) * mm, "end": v(-2033.5, -3767.26) * mm});
            skCircle(sketch, "E370", {"center": v(-2490.7, -3513.26) * mm, "radius": 228.6 * mm});
            skLineSegment(sketch, "E371.bottom", {"start": v(-951.03, -1326.1) * mm, "end": v(-951.03, -767.3) * mm});
            skLineSegment(sketch, "E371.top", {"start": v(-1154.23, -1326.1) * mm, "end": v(-1154.23, -767.3) * mm});
            skLineSegment(sketch, "E371.left", {"start": v(-1154.23, -1326.1) * mm, "end": v(-951.03, -1326.1) * mm});
            skLineSegment(sketch, "E371.right", {"start": v(-1154.23, -767.3) * mm, "end": v(-951.03, -767.3) * mm});
            skEllipse(sketch, "E372", {"center": v(-1403.15, -1046.7) * mm, "majorRadius": 259.08 * mm, "minorRadius": 152.4 * mm, "majorAxis": v(-1, 0)});
            skLineSegment(sketch, "E373", {"start": v(-1154.23, -1046.7) * mm, "end": v(-1403.15, -1046.7) * mm});
            skPoint(sketch, "E373.endSnap0", {"position": v(-1662.23, -1046.7) * mm});
            skLineSegment(sketch, "E374", {"start": v(-493.83, -1326.1) * mm, "end": v(-1052.63, -1326.1) * mm, "construction": true});
            skPoint(sketch, "E374.endSnap0", {"position": v(-1052.63, -767.3) * mm});
            skLineSegment(sketch, "E375", {"start": v(-1662.23, -1046.7) * mm, "end": v(-1154.23, -1046.7) * mm});
            skLineSegment(sketch, "E376.bottom", {"start": v(-2033.5, -3233.86) * mm, "end": v(-1119.1, -3233.86) * mm});
            skLineSegment(sketch, "E376.top", {"start": v(-2033.5, -3767.26) * mm, "end": v(-1119.1, -3767.26) * mm});
            skLineSegment(sketch, "E376.right", {"start": v(-1119.1, -3233.86) * mm, "end": v(-1119.1, -3767.26) * mm});
            skCircle(sketch, "E377", {"center": v(-1576.3, -3513.26) * mm, "radius": 228.6 * mm});
            skLineSegment(sketch, "E378.bottom", {"start": v(-2851.15, -2857.5) * mm, "end": v(-2749.55, -2857.5) * mm});
            skLineSegment(sketch, "E378.top", {"start": v(-2851.15, -3111.5) * mm, "end": v(-2749.55, -3111.5) * mm});
            skLineSegment(sketch, "E378.left", {"start": v(-2851.15, -2857.5) * mm, "end": v(-2851.15, -3111.5) * mm});
            skLineSegment(sketch, "E378.right", {"start": v(-2749.55, -2857.5) * mm, "end": v(-2749.55, -3111.5) * mm});
            skLineSegment(sketch, "E379", {"start": v(-666.75, -3886.2) * mm, "end": v(-666.75, -3771.9) * mm});
            skLineSegment(sketch, "E380", {"start": v(120.65, -3771.9) * mm, "end": v(44.45, -3771.9) * mm});
            skLineSegment(sketch, "E381", {"start": v(44.45, -3771.9) * mm, "end": v(44.45, -3886.2) * mm});
            skLineSegment(sketch, "E382", {"start": v(44.45, -3886.2) * mm, "end": v(120.65, -3886.2) * mm});
            skLineSegment(sketch, "E383", {"start": v(3397.25, 304.8) * mm, "end": v(3295.65, 304.8) * mm});
            skLineSegment(sketch, "E384", {"start": v(3295.65, 304.8) * mm, "end": v(3295.65, 190.5) * mm});
            skLineSegment(sketch, "E385", {"start": v(3295.65, 190.5) * mm, "end": v(3397.25, 190.5) * mm});
            skLineSegment(sketch, "E386", {"start": v(2584.45, 304.8) * mm, "end": v(2584.45, 190.5) * mm});
            skLineSegment(sketch, "E387", {"start": v(2584.45, 190.5) * mm, "end": v(3295.65, 190.5) * mm});
            skLineSegment(sketch, "E388", {"start": v(725.22, -647.7) * mm, "end": v(725.22, 139.7) * mm});
            skLineSegment(sketch, "E389", {"start": v(-895.35, -1562.1) * mm, "end": v(-781.05, -1562.1) * mm});
            skLineSegment(sketch, "E390", {"start": v(-895.35, -2273.3) * mm, "end": v(-781.05, -2273.3) * mm});
            skLineSegment(sketch, "E391", {"start": v(-781.05, -2273.3) * mm, "end": v(-781.05, -2451.1) * mm});
            skLineSegment(sketch, "E392", {"start": v(-895.35, -2273.3) * mm, "end": v(-895.35, -2565.4) * mm});
            skSolve(sketch);
        }
        {
            var Q0;
            Q0=qCreatedBy(makeId("Front.planeOp"),FACE);
            var sketch = newSketch(context, id + "F5", { "sketchPlane" : qUnion([Q0])});
            skLineSegment(sketch, "E393", {"start": v(2381.25, 2641.6) * mm, "end": v(2381.25, 3962.4) * mm});
            skLineSegment(sketch, "E394", {"start": v(-1047.75, 2641.6) * mm, "end": v(2381.25, 2641.6) * mm});
            skLineSegment(sketch, "E395", {"start": v(781.05, 2641.6) * mm, "end": v(781.05, 3022.6) * mm});
            skLineSegment(sketch, "E396", {"start": v(527.05, 3022.6) * mm, "end": v(1035.05, 3022.6) * mm});
            skLineSegment(sketch, "E397", {"start": v(1035.05, 3022.6) * mm, "end": v(1060.45, 3479.8) * mm});
            skLineSegment(sketch, "E398", {"start": v(1060.45, 3479.8) * mm, "end": v(501.65, 3479.8) * mm});
            skLineSegment(sketch, "E399", {"start": v(501.65, 3479.8) * mm, "end": v(527.05, 3022.6) * mm});
            skLineSegment(sketch, "E400", {"start": v(603.25, 2997.2) * mm, "end": v(958.85, 2997.2) * mm});
            skArc(sketch, "E401", {"start": v(603.25, 2997.2) * mm, "mid": v(781.05, 2819.4) * mm, "end": v(958.85, 2997.2) * mm});
            skLineSegment(sketch, "E402", {"start": v(654.05, 2641.6) * mm, "end": v(908.05, 2641.6) * mm});
            skLineSegment(sketch, "E403", {"start": v(908.05, 2641.6) * mm, "end": v(781.05, 2997.2) * mm});
            skLineSegment(sketch, "E404", {"start": v(781.05, 2997.2) * mm, "end": v(654.05, 2641.6) * mm});
            skPoint(sketch, "E405", {"position": v(781.05, 3479.8) * mm});
            skLineSegment(sketch, "E406", {"start": v(1111.25, 3505.2) * mm, "end": v(2025.65, 3505.2) * mm});
            skLineSegment(sketch, "E407", {"start": v(2025.65, 3505.2) * mm, "end": v(2025.65, 2641.6) * mm});
            skLineSegment(sketch, "E408", {"start": v(2025.65, 2641.6) * mm, "end": v(1111.25, 2641.6) * mm});
            skLineSegment(sketch, "E409", {"start": v(1111.25, 2641.6) * mm, "end": v(1111.25, 3505.2) * mm});
            skLineSegment(sketch, "E410", {"start": v(3397.25, 2482.85) * mm, "end": v(3524.25, 2482.85) * mm});
            skLineSegment(sketch, "E411", {"start": v(3524.25, 2482.85) * mm, "end": v(3524.25, 0) * mm});
            skLineSegment(sketch, "E412", {"start": v(3397.25, 0) * mm, "end": v(3397.25, 2482.85) * mm});
            skLineSegment(sketch, "E413", {"start": v(3397.25, 0) * mm, "end": v(3524.25, 0) * mm});
            skLineSegment(sketch, "E414", {"start": v(3346.45, -209.55) * mm, "end": v(3524.25, -209.55) * mm});
            skLineSegment(sketch, "E415", {"start": v(3524.25, -209.55) * mm, "end": v(3524.25, -2343.15) * mm});
            skLineSegment(sketch, "E416", {"start": v(3524.25, -2343.15) * mm, "end": v(3346.45, -2343.15) * mm});
            skLineSegment(sketch, "E417", {"start": v(3346.45, -2343.15) * mm, "end": v(3346.45, -209.55) * mm});
            skLineSegment(sketch, "E418", {"start": v(2381.25, 2641.6) * mm, "end": v(2381.25, 2622.55) * mm});
            skLineSegment(sketch, "E419", {"start": v(2381.25, 2622.55) * mm, "end": v(-1047.75, 2622.55) * mm});
            skLineSegment(sketch, "E420", {"start": v(-1047.75, 2641.6) * mm, "end": v(-1047.75, 2622.55) * mm});
            skLineSegment(sketch, "E421", {"start": v(2381.25, 2622.55) * mm, "end": v(2470.15, 2622.55) * mm});
            skLineSegment(sketch, "E422", {"start": v(2470.15, 2622.55) * mm, "end": v(2470.15, 3976.9) * mm});
            skLineSegment(sketch, "E423", {"start": v(2470.15, 3976.9) * mm, "end": v(2381.25, 4040.58) * mm});
            skLineSegment(sketch, "E424", {"start": v(2381.25, 4040.58) * mm, "end": v(2381.25, 2622.55) * mm});
            skLineSegment(sketch, "E425", {"start": v(4425.95, 2622.55) * mm, "end": v(4425.95, 2482.85) * mm});
            skLineSegment(sketch, "E426", {"start": v(4425.95, 2482.85) * mm, "end": v(-3067.05, 2482.85) * mm});
            skLineSegment(sketch, "E427", {"start": v(-3067.05, 2482.85) * mm, "end": v(-3067.05, 2622.55) * mm});
            skLineSegment(sketch, "E428", {"start": v(-3067.05, 2622.55) * mm, "end": v(4425.95, 2622.55) * mm});
            skLineSegment(sketch, "E429", {"start": v(-3067.05, 2482.85) * mm, "end": v(-2940.3, 2482.85) * mm});
            skLineSegment(sketch, "E430", {"start": v(-2940.3, 2482.85) * mm, "end": v(-2940.3, 0) * mm});
            skLineSegment(sketch, "E431", {"start": v(-2940.3, 0) * mm, "end": v(-3067.05, 0) * mm});
            skLineSegment(sketch, "E432", {"start": v(-3067.05, 0) * mm, "end": v(-3067.05, 2482.85) * mm});
            skLineSegment(sketch, "E433", {"start": v(-628.65, 2482.85) * mm, "end": v(-514.35, 2482.85) * mm});
            skLineSegment(sketch, "E434", {"start": v(-514.35, 2482.85) * mm, "end": v(-514.35, 0) * mm});
            skLineSegment(sketch, "E435", {"start": v(-514.35, 0) * mm, "end": v(-628.65, 0) * mm});
            skLineSegment(sketch, "E436", {"start": v(-628.65, 0) * mm, "end": v(-628.65, 2482.85) * mm});
            skLineSegment(sketch, "E437", {"start": v(-3067.05, -19.05) * mm, "end": v(-3067.05, 0) * mm});
            skLineSegment(sketch, "E438", {"start": v(-3067.05, 0) * mm, "end": v(3524.25, 0) * mm});
            skLineSegment(sketch, "E439", {"start": v(3524.25, 0) * mm, "end": v(3524.25, -19.05) * mm});
            skLineSegment(sketch, "E440", {"start": v(3524.25, -19.05) * mm, "end": v(-3067.05, -19.05) * mm});
            skLineSegment(sketch, "E441", {"start": v(-3067.05, -19.05) * mm, "end": v(-3067.05, -209.55) * mm});
            skLineSegment(sketch, "E442", {"start": v(-3067.05, -209.55) * mm, "end": v(3524.25, -209.55) * mm});
            skLineSegment(sketch, "E443", {"start": v(3524.25, -19.05) * mm, "end": v(3524.25, -209.55) * mm});
            skLineSegment(sketch, "E444", {"start": v(-3067.05, -209.55) * mm, "end": v(-3067.05, -2343.15) * mm});
            skLineSegment(sketch, "E445", {"start": v(-3067.05, -2343.15) * mm, "end": v(-2889.25, -2343.15) * mm});
            skLineSegment(sketch, "E446", {"start": v(-2889.25, -2343.15) * mm, "end": v(-2889.25, -209.55) * mm});
            skLineSegment(sketch, "E447", {"start": v(-2889.25, -209.55) * mm, "end": v(-3067.05, -209.55) * mm});
            skLineSegment(sketch, "E448", {"start": v(-3067.05, -2343.15) * mm, "end": v(-3067.05, -2444.75) * mm});
            skLineSegment(sketch, "E449", {"start": v(3524.25, -2444.75) * mm, "end": v(3524.25, -2343.15) * mm});
            skLineSegment(sketch, "E450", {"start": v(3524.25, -2343.15) * mm, "end": v(-3067.05, -2343.15) * mm});
            skLineSegment(sketch, "E451", {"start": v(-3067.05, -2444.75) * mm, "end": v(3524.25, -2444.75) * mm});
            skLineSegment(sketch, "E452", {"start": v(-3270.25, 2430.1) * mm, "end": v(679.45, 5259.82) * mm});
            skLineSegment(sketch, "E453", {"start": v(679.45, 5259.82) * mm, "end": v(4629.15, 2430.1) * mm});
            skLineSegment(sketch, "E454", {"start": v(4629.15, 2430.1) * mm, "end": v(4629.15, 2555.08) * mm});
            skLineSegment(sketch, "E455", {"start": v(4629.15, 2555.08) * mm, "end": v(679.45, 5384.8) * mm});
            skLineSegment(sketch, "E456", {"start": v(679.45, 5384.8) * mm, "end": v(679.45, 5259.82) * mm});
            skLineSegment(sketch, "E457", {"start": v(679.45, 5384.8) * mm, "end": v(-3270.25, 2555.08) * mm});
            skLineSegment(sketch, "E458", {"start": v(-3270.25, 2555.08) * mm, "end": v(-3270.25, 2430.1) * mm});
            skLineSegment(sketch, "E459", {"start": v(-1149.35, 2622.55) * mm, "end": v(-1149.35, 3949.6) * mm});
            skLineSegment(sketch, "E460", {"start": v(-1149.35, 3949.6) * mm, "end": v(-1047.75, 4022.38) * mm});
            skLineSegment(sketch, "E461", {"start": v(-1047.75, 4022.38) * mm, "end": v(-1047.75, 2622.55) * mm});
            skLineSegment(sketch, "E462", {"start": v(-1047.75, 2622.55) * mm, "end": v(-1149.35, 2622.55) * mm});
            skLineSegment(sketch, "E463", {"start": v(180.3, 4902.2) * mm, "end": v(1178.6, 4902.2) * mm});
            skLineSegment(sketch, "E464", {"start": v(1178.6, 4902.2) * mm, "end": v(1355.87, 4775.2) * mm});
            skLineSegment(sketch, "E465", {"start": v(1355.87, 4775.2) * mm, "end": v(3.03, 4775.2) * mm});
            skLineSegment(sketch, "E466", {"start": v(3.03, 4775.2) * mm, "end": v(180.3, 4902.2) * mm});
            skLineSegment(sketch, "E467", {"start": v(2450.93, 0) * mm, "end": v(3397.25, 0) * mm});
            skLineSegment(sketch, "E468", {"start": v(3397.25, 0) * mm, "end": v(3397.25, 190.5) * mm});
            skLineSegment(sketch, "E469", {"start": v(3397.25, 190.5) * mm, "end": v(2482.85, 190.5) * mm});
            skLineSegment(sketch, "E470", {"start": v(2482.85, 190.5) * mm, "end": v(2482.85, 393.7) * mm});
            skLineSegment(sketch, "E471", {"start": v(2482.85, 393.7) * mm, "end": v(2279.65, 393.7) * mm});
            skLineSegment(sketch, "E472", {"start": v(2279.65, 393.7) * mm, "end": v(2279.65, 596.9) * mm});
            skLineSegment(sketch, "E473", {"start": v(2279.65, 596.9) * mm, "end": v(2076.45, 596.9) * mm});
            skLineSegment(sketch, "E474", {"start": v(2076.45, 596.9) * mm, "end": v(2076.45, 800.1) * mm});
            skLineSegment(sketch, "E475", {"start": v(2076.45, 800.1) * mm, "end": v(1873.25, 800.1) * mm});
            skLineSegment(sketch, "E476", {"start": v(1873.25, 800.1) * mm, "end": v(1873.25, 1003.3) * mm});
            skLineSegment(sketch, "E477", {"start": v(1873.25, 1003.3) * mm, "end": v(1670.05, 1003.3) * mm});
            skLineSegment(sketch, "E478", {"start": v(1670.05, 1003.3) * mm, "end": v(1670.05, 1206.5) * mm});
            skLineSegment(sketch, "E479", {"start": v(1670.05, 1206.5) * mm, "end": v(1466.85, 1206.5) * mm});
            skLineSegment(sketch, "E480", {"start": v(1466.85, 1206.5) * mm, "end": v(1466.85, 1409.7) * mm});
            skLineSegment(sketch, "E481", {"start": v(1466.85, 1409.7) * mm, "end": v(1263.65, 1409.7) * mm});
            skLineSegment(sketch, "E482", {"start": v(1263.65, 1409.7) * mm, "end": v(1263.65, 1612.9) * mm});
            skLineSegment(sketch, "E483", {"start": v(1263.65, 1612.9) * mm, "end": v(1060.45, 1612.9) * mm});
            skLineSegment(sketch, "E484", {"start": v(450.85, 2482.85) * mm, "end": v(450.85, 2265.36) * mm});
            skLineSegment(sketch, "E485", {"start": v(247.65, 2482.85) * mm, "end": v(247.65, 2358.2) * mm});
            skLineSegment(sketch, "E486", {"start": v(247.65, 2358.2) * mm, "end": v(2450.93, 0) * mm});
            skLineSegment(sketch, "E487", {"start": v(1060.45, 1612.9) * mm, "end": v(1060.45, 1830.39) * mm});
            skLineSegment(sketch, "E488", {"start": v(1060.45, 1830.39) * mm, "end": v(857.25, 1830.39) * mm});
            skLineSegment(sketch, "E489", {"start": v(857.25, 1830.39) * mm, "end": v(857.25, 2047.88) * mm});
            skLineSegment(sketch, "E490", {"start": v(857.25, 2047.88) * mm, "end": v(654.05, 2047.88) * mm});
            skLineSegment(sketch, "E491", {"start": v(654.05, 2047.88) * mm, "end": v(654.05, 2265.36) * mm});
            skLineSegment(sketch, "E492", {"start": v(654.05, 2265.36) * mm, "end": v(450.85, 2265.36) * mm});
            skLineSegment(sketch, "E493", {"start": v(3346.45, -2114.55) * mm, "end": v(3346.45, -2343.15) * mm});
            skLineSegment(sketch, "E494", {"start": v(3346.45, -2343.15) * mm, "end": v(2609.6, -2343.15) * mm});
            skLineSegment(sketch, "E495", {"start": v(2609.6, -2343.15) * mm, "end": v(463.55, -139.49) * mm});
            skLineSegment(sketch, "E496", {"start": v(463.55, -139.49) * mm, "end": v(463.55, -19.05) * mm});
            skLineSegment(sketch, "E497", {"start": v(884.06, -387.35) * mm, "end": v(1094.32, -387.35) * mm});
            skLineSegment(sketch, "E498", {"start": v(1094.32, -387.35) * mm, "end": v(1094.32, -603.25) * mm});
            skLineSegment(sketch, "E499", {"start": v(1094.32, -603.25) * mm, "end": v(1304.57, -603.25) * mm});
            skLineSegment(sketch, "E500", {"start": v(1304.57, -603.25) * mm, "end": v(1304.57, -819.15) * mm});
            skLineSegment(sketch, "E501", {"start": v(1304.57, -819.15) * mm, "end": v(1514.83, -819.15) * mm});
            skLineSegment(sketch, "E502", {"start": v(1514.83, -819.15) * mm, "end": v(1514.83, -1035.05) * mm});
            skLineSegment(sketch, "E503", {"start": v(1514.83, -1035.05) * mm, "end": v(1725.08, -1035.05) * mm});
            skLineSegment(sketch, "E504", {"start": v(1725.08, -1035.05) * mm, "end": v(1725.08, -1250.95) * mm});
            skLineSegment(sketch, "E505", {"start": v(1725.08, -1250.95) * mm, "end": v(1935.34, -1250.95) * mm});
            skLineSegment(sketch, "E506", {"start": v(1935.34, -1250.95) * mm, "end": v(1935.34, -1466.85) * mm});
            skLineSegment(sketch, "E507", {"start": v(1935.34, -1466.85) * mm, "end": v(2145.6, -1466.85) * mm});
            skLineSegment(sketch, "E508", {"start": v(2145.6, -1466.85) * mm, "end": v(2145.6, -1682.75) * mm});
            skLineSegment(sketch, "E509", {"start": v(2145.6, -1682.75) * mm, "end": v(2355.85, -1682.75) * mm});
            skLineSegment(sketch, "E510", {"start": v(2355.85, -1682.75) * mm, "end": v(2355.85, -1898.65) * mm});
            skLineSegment(sketch, "E511", {"start": v(2355.85, -1898.65) * mm, "end": v(2584.45, -1898.65) * mm});
            skLineSegment(sketch, "E512", {"start": v(2584.45, -1898.65) * mm, "end": v(2584.45, -2114.55) * mm});
            skLineSegment(sketch, "E513", {"start": v(2584.45, -2114.55) * mm, "end": v(3346.45, -2114.55) * mm});
            skLineSegment(sketch, "E514", {"start": v(884.06, -387.35) * mm, "end": v(884.06, -171.45) * mm});
            skLineSegment(sketch, "E515", {"start": v(884.06, -171.45) * mm, "end": v(673.8, -171.45) * mm});
            skLineSegment(sketch, "E516", {"start": v(673.8, -171.45) * mm, "end": v(673.8, -19.05) * mm});
            skLineSegment(sketch, "E517", {"start": v(673.8, -19.05) * mm, "end": v(463.55, -19.05) * mm});
            skLineSegment(sketch, "E518", {"start": v(450.85, 2482.85) * mm, "end": v(247.65, 2482.85) * mm});
            skLineSegment(sketch, "E519", {"start": v(450.85, 2265.36) * mm, "end": v(654.05, 2047.88) * mm, "construction": true});
            skLineSegment(sketch, "E520", {"start": v(673.8, -171.45) * mm, "end": v(884.06, -387.35) * mm, "construction": true});
            skLineSegment(sketch, "E521", {"start": v(-2863.85, -209.55) * mm, "end": v(-2863.85, -2343.15) * mm});
            skLineSegment(sketch, "E522", {"start": v(-2863.85, -2343.15) * mm, "end": v(-2762.25, -2343.15) * mm});
            skLineSegment(sketch, "E523", {"start": v(-2762.25, -2343.15) * mm, "end": v(-2762.25, -209.55) * mm});
            skLineSegment(sketch, "E524", {"start": v(-2762.25, -209.55) * mm, "end": v(-2863.85, -209.55) * mm});
            skLineSegment(sketch, "E525", {"start": v(-44.45, -209.55) * mm, "end": v(69.85, -209.55) * mm});
            skLineSegment(sketch, "E526", {"start": v(69.85, -209.55) * mm, "end": v(69.85, -400.05) * mm});
            skLineSegment(sketch, "E527", {"start": v(69.85, -400.05) * mm, "end": v(-44.45, -400.05) * mm});
            skLineSegment(sketch, "E528", {"start": v(-44.45, -400.05) * mm, "end": v(-44.45, -209.55) * mm});
            skLineSegment(sketch, "E529", {"start": v(-44.45, -400.05) * mm, "end": v(-44.45, -2343.15) * mm});
            skLineSegment(sketch, "E530", {"start": v(-44.45, -2343.15) * mm, "end": v(69.85, -2343.15) * mm});
            skLineSegment(sketch, "E531", {"start": v(69.85, -2343.15) * mm, "end": v(69.85, -400.05) * mm});
            skSolve(sketch);
        }
        {
            var Q0;
            {var subQ15=sQuery(id+"F3.wireOp",EDGE,"E178.left");Q0=makeQuery(id+"F3.imprint","IMPRINT",FACE,{"disambiguationData":[TD([[makeQuery(id+"F3.imprint","IMPRINT",EDGE,{"derivedFrom":subQ15}),1.0]])]});}
            var Q1;
            {var subQ5=sQuery(id+"F3.wireOp",EDGE,"E181.0");Q1=makeQuery(id+"F3.imprint","IMPRINT",FACE,{"disambiguationData":[TD([[makeQuery(id+"F3.imprint","IMPRINT",EDGE,{"derivedFrom":subQ5}),1.0]])]});}
            var Q2;
            {var subQ4=sQuery(id+"F3.wireOp",EDGE,"E185.0");Q2=makeQuery(id+"F3.imprint","IMPRINT",FACE,{"disambiguationData":[TD([[makeQuery(id+"F3.imprint","IMPRINT",EDGE,{"derivedFrom":subQ4}),1.0]])]});}
            var Q3;
            {var subQ5=sQuery(id+"F3.wireOp",EDGE,"E239.right");Q3=makeQuery(id+"F3.imprint","IMPRINT",FACE,{"disambiguationData":[TD([[makeQuery(id+"F3.imprint","IMPRINT",EDGE,{"derivedFrom":subQ5}),1.0]])]});}
            var Q4;
            {var subQ0=sQuery(id+"F3.wireOp",EDGE,"E190");Q4=makeQuery(id+"F3.imprint","IMPRINT",FACE,{"disambiguationData":[TD([[makeQuery(id+"F3.imprint","IMPRINT",EDGE,{"derivedFrom":subQ0}),-1.0]])]});}
            var Q5;
            {var subQ10=sQuery(id+"F3.wireOp",EDGE,"E247");Q5=makeQuery(id+"F3.imprint","IMPRINT",FACE,{"disambiguationData":[TD([[makeQuery(id+"F3.imprint","IMPRINT",EDGE,{"derivedFrom":subQ10}),-1.0]])]});}
            var Q6;
            Q6=makeQuery(id+"F3.imprint","IMPRINT",FACE,{"disambiguationData":[TD([[makeQuery(id+"F3.imprint","IMPRINT",EDGE,{"derivedFrom":sQuery(id+"F3.wireOp",EDGE,"E248")}),1.0]])]});
            var Q7;
            {var subQ0=sQuery(id+"F3.wireOp",EDGE,"E232");Q7=makeQuery(id+"F3.imprint","IMPRINT",FACE,{"disambiguationData":[TD([[makeQuery(id+"F3.imprint","IMPRINT",EDGE,{"derivedFrom":subQ0}),-1.0]])]});}
            var Q8;
            {var subQ5=sQuery(id+"F3.wireOp",EDGE,"E229");Q8=makeQuery(id+"F3.imprint","IMPRINT",FACE,{"disambiguationData":[TD([[makeQuery(id+"F3.imprint","IMPRINT",EDGE,{"derivedFrom":subQ5}),-1.0]])]});}
            var Q9;
            {var subQ0=sQuery(id+"F3.wireOp",EDGE,"E216");Q9=makeQuery(id+"F3.imprint","IMPRINT",FACE,{"disambiguationData":[TD([[makeQuery(id+"F3.imprint","IMPRINT",EDGE,{"derivedFrom":subQ0}),1.0]])]});}
            var Q10;
            {var subQ2=sQuery(id+"F3.wireOp",EDGE,"E273");Q10=makeQuery(id+"F3.imprint","IMPRINT",FACE,{"disambiguationData":[TD([[makeQuery(id+"F3.imprint","IMPRINT",EDGE,{"derivedFrom":subQ2}),1.0]])]});}
            var Q11;
            Q11=makeQuery(id+"F3.imprint","IMPRINT",FACE,{"disambiguationData":[TD([[makeQuery(id+"F3.imprint","IMPRINT",EDGE,{"derivedFrom":sQuery(id+"F3.wireOp",EDGE,"E266")}),-1.0]])]});
            var Q12;
            {var subQ8=sQuery(id+"F3.wireOp",EDGE,"E264");Q12=makeQuery(id+"F3.imprint","IMPRINT",FACE,{"disambiguationData":[TD([[makeQuery(id+"F3.imprint","IMPRINT",EDGE,{"derivedFrom":subQ8}),-1.0]])]});}
            var Q13;
            Q13=makeQuery(id+"F3.imprint","IMPRINT",FACE,{"disambiguationData":[TD([[makeQuery(id+"F3.imprint","IMPRINT",EDGE,{"derivedFrom":sQuery(id+"F3.wireOp",EDGE,"E256")}),-1.0]])]});
            var Q14;
            Q14=makeQuery(id+"F3.imprint","IMPRINT",FACE,{"disambiguationData":[TD([[makeQuery(id+"F3.imprint","IMPRINT",EDGE,{"derivedFrom":sQuery(id+"F3.wireOp",EDGE,"E239.bottom")}),1.0]])]});
            var Q15;
            {var subQ0=sQuery(id+"F3.wireOp",EDGE,"E234");Q15=makeQuery(id+"F3.imprint","IMPRINT",FACE,{"disambiguationData":[TD([[makeQuery(id+"F3.imprint","IMPRINT",EDGE,{"derivedFrom":subQ0}),-1.0]])]});}
            extrude(context, id + "F6", {"entities" : qUnion([Q0, Q1, Q2, Q3, Q4, Q5, Q6, Q7, Q8, Q9, Q10, Q11, Q12, Q13, Q14, Q15]), "depth" : 2.54 * mm});
        }
        {
            var Q0;
            Q0=makeQuery(id+"F3.imprint","IMPRINT",FACE,{"disambiguationData":[TD([[makeQuery(id+"F3.imprint","IMPRINT",EDGE,{"derivedFrom":sQuery(id+"F3.wireOp",EDGE,"E237.bottom")}),-1.0]])]});
            var Q1;
            {var subQ0=sQuery(id+"F3.wireOp",EDGE,"E245");var subQ4=makeQuery(id+"F3.imprint","IMPRINT",VERTEX,{"derivedFrom":subQ0});Q1=makeQuery(id+"F3.imprint","IMPRINT",FACE,{"disambiguationData":[TD([[makeQuery(id+"F3.imprint","IMPRINT",EDGE,{"disambiguationData":[TD([[subQ4,1.0]])],"derivedFrom":subQ0}),1.0]])]});}
            var Q2;
            {var subQ0=sQuery(id+"F3.wireOp",EDGE,"E245");var subQ4=makeQuery(id+"F3.imprint","IMPRINT",VERTEX,{"derivedFrom":subQ0});Q2=makeQuery(id+"F3.imprint","IMPRINT",FACE,{"disambiguationData":[TD([[makeQuery(id+"F3.imprint","IMPRINT",EDGE,{"disambiguationData":[TD([[subQ4,1.0]])],"derivedFrom":subQ0}),-1.0]])]});}
            var Q3;
            Q3=makeQuery(id+"F3.imprint","IMPRINT",FACE,{"disambiguationData":[TD([[makeQuery(id+"F3.imprint","IMPRINT",EDGE,{"derivedFrom":sQuery(id+"F3.wireOp",EDGE,"E241.bottom")}),1.0]])]});
            var Q4;
            {var subQ0=sQuery(id+"F3.wireOp",EDGE,"E242");var subQ1=sQuery(id+"F3.wireOp",EDGE,"E241.top");var subQ2=makeQuery(id+"F3.imprint","INTERSECT",VERTEX,{"disambiguationData":[OD(0.0)],"derivedFrom":[subQ1,subQ0]});Q4=makeQuery(id+"F3.imprint","IMPRINT",FACE,{"disambiguationData":[TD([[makeQuery(id+"F3.imprint","IMPRINT",EDGE,{"disambiguationData":[TD([[subQ2,-1.0]])],"derivedFrom":subQ1}),-1.0]])]});}
            var Q5;
            {var subQ0=sQuery(id+"F3.wireOp",EDGE,"E245");var subQ1=sQuery(id+"F3.wireOp",EDGE,"E241.top");var subQ2=makeQuery(id+"F3.imprint","INTERSECT",VERTEX,{"derivedFrom":[subQ1,subQ0]});Q5=makeQuery(id+"F3.imprint","IMPRINT",FACE,{"disambiguationData":[TD([[makeQuery(id+"F3.imprint","IMPRINT",EDGE,{"disambiguationData":[TD([[subQ2,-1.0]])],"derivedFrom":subQ1}),-1.0]])]});}
            extrude(context, id + "F7", {"entities" : qUnion([Q0, Q1, Q2, Q3, Q4, Q5]), "oppositeDirection" : true, "depth" : 25.4 * mm});
        }
        {
            var Q0;
            {var subQ0=sQuery(id+"F3.wireOp",EDGE,"E178.left");Q0=makeQuery(id+"F3.imprint","IMPRINT",FACE,{"disambiguationData":[TD([[makeQuery(id+"F3.imprint","IMPRINT",EDGE,{"derivedFrom":subQ0}),-1.0]])]});}
            var Q1;
            {var subQ8=sQuery(id+"F3.wireOp",EDGE,"E178.right");Q1=makeQuery(id+"F3.imprint","IMPRINT",FACE,{"disambiguationData":[TD([[makeQuery(id+"F3.imprint","IMPRINT",EDGE,{"derivedFrom":subQ8}),1.0]])]});}
            var Q2;
            {var subQ5=sQuery(id+"F3.wireOp",EDGE,"E236");Q2=makeQuery(id+"F3.imprint","IMPRINT",FACE,{"disambiguationData":[TD([[makeQuery(id+"F3.imprint","IMPRINT",EDGE,{"derivedFrom":subQ5}),1.0]])]});}
            var Q3;
            {var subQ9=sQuery(id+"F3.wireOp",EDGE,"E217");Q3=makeQuery(id+"F3.imprint","IMPRINT",FACE,{"disambiguationData":[TD([[makeQuery(id+"F3.imprint","IMPRINT",EDGE,{"derivedFrom":subQ9}),1.0]])]});}
            var Q4;
            Q4=makeQuery(id+"F3.imprint","IMPRINT",FACE,{"disambiguationData":[TD([[makeQuery(id+"F3.imprint","IMPRINT",EDGE,{"derivedFrom":sQuery(id+"F3.wireOp",EDGE,"E203")}),-1.0]])]});
            var Q5;
            Q5=makeQuery(id+"F3.imprint","IMPRINT",FACE,{"disambiguationData":[TD([[makeQuery(id+"F3.imprint","IMPRINT",EDGE,{"derivedFrom":sQuery(id+"F3.wireOp",EDGE,"E238")}),1.0]])]});
            var Q6;
            {var subQ4=sQuery(id+"F3.wireOp",EDGE,"E234");Q6=makeQuery(id+"F3.imprint","IMPRINT",FACE,{"disambiguationData":[TD([[makeQuery(id+"F3.imprint","IMPRINT",EDGE,{"derivedFrom":subQ4}),1.0]])]});}
            extrude(context, id + "F8", {"entities" : qUnion([Q0, Q1, Q2, Q3, Q4, Q5, Q6]), "depth" : 6.35 * mm});
        }
        {
            var Q0;
            Q0=makeQuery(id+"F5.imprint","IMPRINT",FACE,{"disambiguationData":[TD([[makeQuery(id+"F5.imprint","IMPRINT",EDGE,{"derivedFrom":sQuery(id+"F5.wireOp",EDGE,"E441")}),1.0]])]});
            var Q1;
            {var subQ0=sQuery(id+"F5.wireOp",EDGE,"E444");Q1=makeQuery(id+"F5.imprint","IMPRINT",FACE,{"disambiguationData":[TD([[makeQuery(id+"F5.imprint","IMPRINT",EDGE,{"derivedFrom":subQ0}),1.0]])]});}
            var Q2;
            {var subQ4=sQuery(id+"F5.wireOp",EDGE,"E448");Q2=makeQuery(id+"F5.imprint","IMPRINT",FACE,{"disambiguationData":[TD([[makeQuery(id+"F5.imprint","IMPRINT",EDGE,{"derivedFrom":subQ4}),1.0]])]});}
            var Q3;
            {var subQ1=sQuery(id+"F5.wireOp",EDGE,"E415");Q3=makeQuery(id+"F5.imprint","IMPRINT",FACE,{"disambiguationData":[TD([[makeQuery(id+"F5.imprint","IMPRINT",EDGE,{"derivedFrom":subQ1}),-1.0]])]});}
            var Q4;
            Q4=makeQuery(id+"F5.imprint","IMPRINT",FACE,{"disambiguationData":[TD([[makeQuery(id+"F5.imprint","IMPRINT",EDGE,{"derivedFrom":sQuery(id+"F5.wireOp",EDGE,"E429")}),-1.0]])]});
            var Q5;
            {var subQ1=sQuery(id+"F5.wireOp",EDGE,"E411");Q5=makeQuery(id+"F5.imprint","IMPRINT",FACE,{"disambiguationData":[TD([[makeQuery(id+"F5.imprint","IMPRINT",EDGE,{"derivedFrom":subQ1}),-1.0]])]});}
            var Q6;
            {var subQ1=sQuery(id+"F5.wireOp",EDGE,"E427");Q6=makeQuery(id+"F5.imprint","IMPRINT",FACE,{"disambiguationData":[TD([[makeQuery(id+"F5.imprint","IMPRINT",EDGE,{"derivedFrom":subQ1}),-1.0]])]});}
            var Q7;
            {var subQ0=sQuery(id+"F5.wireOp",EDGE,"E456");Q7=makeQuery(id+"F5.imprint","IMPRINT",FACE,{"disambiguationData":[TD([[makeQuery(id+"F5.imprint","IMPRINT",EDGE,{"derivedFrom":subQ0}),-1.0]])]});}
            var Q8;
            {var subQ6=sQuery(id+"F5.wireOp",EDGE,"E454");Q8=makeQuery(id+"F5.imprint","IMPRINT",FACE,{"disambiguationData":[TD([[makeQuery(id+"F5.imprint","IMPRINT",EDGE,{"derivedFrom":subQ6}),1.0]])]});}
            var Q9;
            Q9=makeQuery(id+"F5.imprint","IMPRINT",FACE,{"disambiguationData":[TD([[makeQuery(id+"F5.imprint","IMPRINT",EDGE,{"derivedFrom":sQuery(id+"F5.wireOp",EDGE,"E433")}),-1.0]])]});
            var Q10;
            Q10=makeQuery(id+"F5.imprint","IMPRINT",FACE,{"disambiguationData":[TD([[makeQuery(id+"F5.imprint","IMPRINT",EDGE,{"derivedFrom":sQuery(id+"F5.wireOp",EDGE,"E493")}),-1.0]])]});
            var Q11;
            Q11=makeQuery(id+"F5.imprint","IMPRINT",FACE,{"disambiguationData":[TD([[makeQuery(id+"F5.imprint","IMPRINT",EDGE,{"derivedFrom":sQuery(id+"F5.wireOp",EDGE,"E467")}),1.0]])]});
            var Q12;
            {var subQ3=sQuery(id+"F5.wireOp",EDGE,"E437");Q12=makeQuery(id+"F5.imprint","IMPRINT",FACE,{"disambiguationData":[TD([[makeQuery(id+"F5.imprint","IMPRINT",EDGE,{"derivedFrom":subQ3}),-1.0]])]});}
            var Q13;
            {var subQ8=sQuery(id+"F5.wireOp",EDGE,"E429");Q13=makeQuery(id+"F5.imprint","IMPRINT",FACE,{"disambiguationData":[TD([[makeQuery(id+"F5.imprint","IMPRINT",EDGE,{"derivedFrom":subQ8}),1.0]])]});}
            var Q14;
            {var subQ0=sQuery(id+"F5.wireOp",EDGE,"E428");var subQ1=sQuery(id+"F5.wireOp",EDGE,"E425");var subQ2=makeQuery(id+"F5.imprint","INTERSECT",VERTEX,{"derivedFrom":[subQ1,subQ0]});Q14=makeQuery(id+"F5.imprint","IMPRINT",FACE,{"disambiguationData":[TD([[makeQuery(id+"F5.imprint","IMPRINT",EDGE,{"disambiguationData":[TD([[subQ2,-1.0]])],"derivedFrom":subQ1}),-1.0]])]});}
            var Q15;
            Q15=makeQuery(id+"F5.imprint","IMPRINT",FACE,{"disambiguationData":[TD([[makeQuery(id+"F5.imprint","IMPRINT",EDGE,{"derivedFrom":sQuery(id+"F5.wireOp",EDGE,"E521")}),1.0]])]});
            var Q16;
            {var subQ1=sQuery(id+"F5.wireOp",EDGE,"E443");Q16=makeQuery(id+"F5.imprint","IMPRINT",FACE,{"disambiguationData":[TD([[makeQuery(id+"F5.imprint","IMPRINT",EDGE,{"derivedFrom":subQ1}),-1.0]])]});}
            var Q17;
            {var subQ4=sQuery(id+"F5.wireOp",EDGE,"E496");Q17=makeQuery(id+"F5.imprint","IMPRINT",FACE,{"disambiguationData":[TD([[makeQuery(id+"F5.imprint","IMPRINT",EDGE,{"derivedFrom":subQ4}),-1.0]])]});}
            var Q18;
            Q18=makeQuery(id+"F5.imprint","IMPRINT",FACE,{"disambiguationData":[TD([[makeQuery(id+"F5.imprint","IMPRINT",EDGE,{"derivedFrom":sQuery(id+"F5.wireOp",EDGE,"E527")}),1.0]])]});
            var Q19;
            Q19=makeQuery(id+"F5.imprint","IMPRINT",FACE,{"disambiguationData":[TD([[makeQuery(id+"F5.imprint","IMPRINT",EDGE,{"derivedFrom":sQuery(id+"F5.wireOp",EDGE,"E525")}),-1.0]])]});
            extrude(context, id + "F9", {"entities" : qUnion([Q0, Q1, Q2, Q3, Q4, Q5, Q6, Q7, Q8, Q9, Q10, Q11, Q12, Q13, Q14, Q15, Q16, Q17, Q18, Q19]), "depth" : 25.4 * mm});
        }
        {
            var Q0;
            Q0=makeQuery(id+"F5.imprint","IMPRINT",FACE,{"disambiguationData":[TD([[makeQuery(id+"F5.imprint","IMPRINT",EDGE,{"derivedFrom":sQuery(id+"F5.wireOp",EDGE,"E459")}),-1.0]])]});
            var Q1;
            Q1=makeQuery(id+"F5.imprint","IMPRINT",FACE,{"disambiguationData":[TD([[makeQuery(id+"F5.imprint","IMPRINT",EDGE,{"derivedFrom":sQuery(id+"F5.wireOp",EDGE,"E463")}),-1.0]])]});
            var Q2;
            {var subQ7=sQuery(id+"F5.wireOp",EDGE,"E422");Q2=makeQuery(id+"F5.imprint","IMPRINT",FACE,{"disambiguationData":[TD([[makeQuery(id+"F5.imprint","IMPRINT",EDGE,{"derivedFrom":subQ7}),1.0]])]});}
            var Q3;
            {var subQ0=sQuery(id+"F5.wireOp",EDGE,"E394");var subQ7=makeQuery(id+"F5.imprint","INTERSECT",VERTEX,{"derivedFrom":[sQuery(id+"F5.wireOp",EDGE,"E404"),subQ0]});Q3=makeQuery(id+"F5.imprint","IMPRINT",FACE,{"disambiguationData":[TD([[makeQuery(id+"F5.imprint","IMPRINT",EDGE,{"disambiguationData":[TD([[subQ7,1.0]])],"derivedFrom":subQ0}),-1.0]])]});}
            var Q4;
            Q4=makeQuery(id+"F5.imprint","IMPRINT",FACE,{"disambiguationData":[TD([[makeQuery(id+"F5.imprint","IMPRINT",EDGE,{"derivedFrom":sQuery(id+"F5.wireOp",EDGE,"E406")}),-1.0]])]});
            var Q5;
            {var subQ0=sQuery(id+"F5.wireOp",EDGE,"E394");var subQ1=sQuery(id+"F5.wireOp",EDGE,"E395");var subQ2=makeQuery(id+"F5.imprint","INTERSECT",VERTEX,{"derivedFrom":[subQ1,subQ0]});Q5=makeQuery(id+"F5.imprint","IMPRINT",FACE,{"disambiguationData":[TD([[makeQuery(id+"F5.imprint","IMPRINT",EDGE,{"disambiguationData":[TD([[subQ2,-1.0]])],"derivedFrom":subQ1}),-1.0]])]});}
            var Q6;
            {var subQ0=sQuery(id+"F5.wireOp",EDGE,"E394");var subQ1=sQuery(id+"F5.wireOp",EDGE,"E395");var subQ2=makeQuery(id+"F5.imprint","INTERSECT",VERTEX,{"derivedFrom":[subQ1,subQ0]});Q6=makeQuery(id+"F5.imprint","IMPRINT",FACE,{"disambiguationData":[TD([[makeQuery(id+"F5.imprint","IMPRINT",EDGE,{"disambiguationData":[TD([[subQ2,-1.0]])],"derivedFrom":subQ1}),1.0]])]});}
            var Q7;
            {var subQ1=sQuery(id+"F5.wireOp",EDGE,"E395");var subQ3=sQuery(id+"F5.wireOp",EDGE,"E401");var subQ4=makeQuery(id+"F5.imprint","INTERSECT",VERTEX,{"derivedFrom":[subQ1,subQ3]});Q7=makeQuery(id+"F5.imprint","IMPRINT",FACE,{"disambiguationData":[TD([[makeQuery(id+"F5.imprint","IMPRINT",EDGE,{"disambiguationData":[TD([[subQ4,1.0]])],"derivedFrom":subQ3}),1.0]])]});}
            var Q8;
            {var subQ1=sQuery(id+"F5.wireOp",EDGE,"E395");var subQ3=sQuery(id+"F5.wireOp",EDGE,"E401");var subQ4=makeQuery(id+"F5.imprint","INTERSECT",VERTEX,{"derivedFrom":[subQ1,subQ3]});Q8=makeQuery(id+"F5.imprint","IMPRINT",FACE,{"disambiguationData":[TD([[makeQuery(id+"F5.imprint","IMPRINT",EDGE,{"disambiguationData":[TD([[subQ4,-1.0]])],"derivedFrom":subQ3}),1.0]])]});}
            var Q9;
            {var subQ0=sQuery(id+"F5.wireOp",EDGE,"E401");var subQ1=sQuery(id+"F5.wireOp",EDGE,"E400");var subQ2=makeQuery(id+"F5.imprint","INTERSECT",VERTEX,{"disambiguationData":[OD(0.0)],"derivedFrom":[subQ1,subQ0]});Q9=makeQuery(id+"F5.imprint","IMPRINT",FACE,{"disambiguationData":[TD([[makeQuery(id+"F5.imprint","IMPRINT",EDGE,{"disambiguationData":[TD([[subQ2,-1.0]])],"derivedFrom":subQ0}),1.0]])]});}
            var Q10;
            {var subQ0=sQuery(id+"F5.wireOp",EDGE,"E401");var subQ1=sQuery(id+"F5.wireOp",EDGE,"E400");var subQ2=makeQuery(id+"F5.imprint","INTERSECT",VERTEX,{"disambiguationData":[OD(1.0)],"derivedFrom":[subQ1,subQ0]});Q10=makeQuery(id+"F5.imprint","IMPRINT",FACE,{"disambiguationData":[TD([[makeQuery(id+"F5.imprint","IMPRINT",EDGE,{"disambiguationData":[TD([[subQ2,1.0]])],"derivedFrom":subQ0}),1.0]])]});}
            var Q11;
            {var subQ0=sQuery(id+"F5.wireOp",EDGE,"E397");Q11=makeQuery(id+"F5.imprint","IMPRINT",FACE,{"disambiguationData":[TD([[makeQuery(id+"F5.imprint","IMPRINT",EDGE,{"derivedFrom":subQ0}),1.0]])]});}
            extrude(context, id + "F10", {"entities" : qUnion([Q0, Q1, Q2, Q3, Q4, Q5, Q6, Q7, Q8, Q9, Q10, Q11]), "depth" : 25.4 * mm, "hasSecondDirection" : true, "secondDirectionOppositeDirection" : true, "secondDirectionDepth" : 25.4 * mm});
        }
        {
            var Q0;
            {var subQ3=sQuery(id+"F5.wireOp",EDGE,"E459");Q0=makeQuery(id+"F5.imprint","IMPRINT",FACE,{"disambiguationData":[TD([[makeQuery(id+"F5.imprint","IMPRINT",EDGE,{"derivedFrom":subQ3}),1.0]])]});}
            var Q1;
            {var subQ21=sQuery(id+"F5.wireOp",EDGE,"E397");Q1=makeQuery(id+"F5.imprint","IMPRINT",FACE,{"disambiguationData":[TD([[makeQuery(id+"F5.imprint","IMPRINT",EDGE,{"derivedFrom":subQ21}),-1.0]])]});}
            var Q2;
            {var subQ3=sQuery(id+"F5.wireOp",EDGE,"E463");Q2=makeQuery(id+"F5.imprint","IMPRINT",FACE,{"disambiguationData":[TD([[makeQuery(id+"F5.imprint","IMPRINT",EDGE,{"derivedFrom":subQ3}),1.0]])]});}
            var Q3;
            {var subQ0=sQuery(id+"F5.wireOp",EDGE,"E422");Q3=makeQuery(id+"F5.imprint","IMPRINT",FACE,{"disambiguationData":[TD([[makeQuery(id+"F5.imprint","IMPRINT",EDGE,{"derivedFrom":subQ0}),-1.0]])]});}
            var Q4;
            {var subQ2=sQuery(id+"F5.wireOp",EDGE,"E412");Q4=makeQuery(id+"F5.imprint","IMPRINT",FACE,{"disambiguationData":[TD([[makeQuery(id+"F5.imprint","IMPRINT",EDGE,{"derivedFrom":subQ2}),1.0]])]});}
            var Q5;
            {var subQ2=sQuery(id+"F5.wireOp",EDGE,"E434");Q5=makeQuery(id+"F5.imprint","IMPRINT",FACE,{"disambiguationData":[TD([[makeQuery(id+"F5.imprint","IMPRINT",EDGE,{"derivedFrom":subQ2}),1.0]])]});}
            var Q6;
            {var subQ0=sQuery(id+"F5.wireOp",EDGE,"E430");Q6=makeQuery(id+"F5.imprint","IMPRINT",FACE,{"disambiguationData":[TD([[makeQuery(id+"F5.imprint","IMPRINT",EDGE,{"derivedFrom":subQ0}),1.0]])]});}
            var Q7;
            {var subQ2=sQuery(id+"F5.wireOp",EDGE,"E446");Q7=makeQuery(id+"F5.imprint","IMPRINT",FACE,{"disambiguationData":[TD([[makeQuery(id+"F5.imprint","IMPRINT",EDGE,{"derivedFrom":subQ2}),-1.0]])]});}
            var Q8;
            {var subQ0=sQuery(id+"F5.wireOp",EDGE,"E417");Q8=makeQuery(id+"F5.imprint","IMPRINT",FACE,{"disambiguationData":[TD([[makeQuery(id+"F5.imprint","IMPRINT",EDGE,{"derivedFrom":subQ0}),1.0]])]});}
            var Q9;
            {var subQ0=sQuery(id+"F5.wireOp",EDGE,"E523");Q9=makeQuery(id+"F5.imprint","IMPRINT",FACE,{"disambiguationData":[TD([[makeQuery(id+"F5.imprint","IMPRINT",EDGE,{"derivedFrom":subQ0}),-1.0]])]});}
            var Q10;
            {var subQ0=sQuery(id+"F5.wireOp",EDGE,"E526");Q10=makeQuery(id+"F5.imprint","IMPRINT",FACE,{"disambiguationData":[TD([[makeQuery(id+"F5.imprint","IMPRINT",EDGE,{"derivedFrom":subQ0}),1.0]])]});}
            extrude(context, id + "F11", {"entities" : qUnion([Q0, Q1, Q2, Q3, Q4, Q5, Q6, Q7, Q8, Q9, Q10]), "depth" : 6.35 * mm});
        }
        {
            var Q0;
            Q0=makeQuery(id+"F4.imprint","IMPRINT",FACE,{"disambiguationData":[TD([[makeQuery(id+"F4.imprint","IMPRINT",EDGE,{"derivedFrom":sQuery(id+"F4.wireOp",EDGE,"E279")}),-1.0]])]});
            var Q1;
            Q1=makeQuery(id+"F4.imprint","IMPRINT",FACE,{"disambiguationData":[TD([[makeQuery(id+"F4.imprint","IMPRINT",EDGE,{"derivedFrom":sQuery(id+"F4.wireOp",EDGE,"E314")}),-1.0]])]});
            extrude(context, id + "F12", {"entities" : qUnion([Q0, Q1]), "depth" : 25.4 * mm});
        }
        {
            var Q0;
            Q0=makeQuery(id+"F4.imprint","IMPRINT",FACE,{"disambiguationData":[TD([[makeQuery(id+"F4.imprint","IMPRINT",EDGE,{"derivedFrom":sQuery(id+"F4.wireOp",EDGE,"E369.bottom")}),-1.0]])]});
            var Q1;
            Q1=makeQuery(id+"F4.imprint","IMPRINT",FACE,{"disambiguationData":[TD([[makeQuery(id+"F4.imprint","IMPRINT",EDGE,{"derivedFrom":sQuery(id+"F4.wireOp",EDGE,"E376.bottom")}),-1.0]])]});
            var Q2;
            {var subQ0=sQuery(id+"F4.wireOp",EDGE,"E375");var subQ4=makeQuery(id+"F4.imprint","IMPRINT",VERTEX,{"derivedFrom":subQ0});Q2=makeQuery(id+"F4.imprint","IMPRINT",FACE,{"disambiguationData":[TD([[makeQuery(id+"F4.imprint","IMPRINT",EDGE,{"disambiguationData":[TD([[subQ4,1.0]])],"derivedFrom":subQ0}),-1.0]])]});}
            var Q3;
            {var subQ0=sQuery(id+"F4.wireOp",EDGE,"E375");var subQ4=makeQuery(id+"F4.imprint","IMPRINT",VERTEX,{"derivedFrom":subQ0});Q3=makeQuery(id+"F4.imprint","IMPRINT",FACE,{"disambiguationData":[TD([[makeQuery(id+"F4.imprint","IMPRINT",EDGE,{"disambiguationData":[TD([[subQ4,1.0]])],"derivedFrom":subQ0}),1.0]])]});}
            var Q4;
            Q4=makeQuery(id+"F4.imprint","IMPRINT",FACE,{"disambiguationData":[TD([[makeQuery(id+"F4.imprint","IMPRINT",EDGE,{"derivedFrom":sQuery(id+"F4.wireOp",EDGE,"E371.bottom")}),1.0]])]});
            var Q5;
            {var subQ0=sQuery(id+"F4.wireOp",EDGE,"E371.top");var subQ1=makeQuery(id+"F4.imprint","INTERSECT",VERTEX,{"derivedFrom":[subQ0,sQuery(id+"F4.wireOp",EDGE,"E375")]});Q5=makeQuery(id+"F4.imprint","IMPRINT",FACE,{"disambiguationData":[TD([[makeQuery(id+"F4.imprint","IMPRINT",EDGE,{"disambiguationData":[TD([[subQ1,1.0]])],"derivedFrom":subQ0}),-1.0]])]});}
            var Q6;
            Q6=makeQuery(id+"F4.imprint","IMPRINT",FACE,{"disambiguationData":[TD([[makeQuery(id+"F4.imprint","IMPRINT",EDGE,{"derivedFrom":sQuery(id+"F4.wireOp",EDGE,"E358")}),-1.0]])]});
            extrude(context, id + "F13", {"entities" : qUnion([Q0, Q1, Q2, Q3, Q4, Q5, Q6]), "depth" : 25.4 * mm});
        }
        {
            var Q0;
            Q0=makeQuery(id+"F4.imprint","IMPRINT",FACE,{"disambiguationData":[TD([[makeQuery(id+"F4.imprint","IMPRINT",EDGE,{"derivedFrom":sQuery(id+"F4.wireOp",EDGE,"E291")}),-1.0]])]});
            var Q1;
            Q1=makeQuery(id+"F4.imprint","IMPRINT",FACE,{"disambiguationData":[TD([[makeQuery(id+"F4.imprint","IMPRINT",EDGE,{"derivedFrom":sQuery(id+"F4.wireOp",EDGE,"E378.bottom")}),-1.0]])]});
            extrude(context, id + "F14", {"entities" : qUnion([Q0, Q1]), "depth" : 6.35 * mm});
        }
        {
            var Q0;
            {var subQ7=sQuery(id+"F2.wireOp",EDGE,"E0.bottom");Q0=makeQuery(id+"F2.imprint","IMPRINT",FACE,{"disambiguationData":[TD([[makeQuery(id+"F2.imprint","IMPRINT",EDGE,{"derivedFrom":subQ7}),-1.0]])]});}
            var Q1;
            Q1=makeQuery(id+"F2.imprint","IMPRINT",FACE,{"disambiguationData":[TD([[makeQuery(id+"F2.imprint","IMPRINT",EDGE,{"derivedFrom":sQuery(id+"F2.wireOp",EDGE,"E0.right")}),-1.0]])]});
            var Q2;
            {var subQ3=sQuery(id+"F2.wireOp",EDGE,"E84.trimOffspring");Q2=makeQuery(id+"F2.imprint","IMPRINT",FACE,{"disambiguationData":[TD([[makeQuery(id+"F2.imprint","IMPRINT",EDGE,{"derivedFrom":subQ3}),1.0]])]});}
            var Q3;
            {var subQ3=sQuery(id+"F2.wireOp",EDGE,"E86.trimOffspring");Q3=makeQuery(id+"F2.imprint","IMPRINT",FACE,{"disambiguationData":[TD([[makeQuery(id+"F2.imprint","IMPRINT",EDGE,{"derivedFrom":subQ3}),-1.0]])]});}
            var Q4;
            {var subQ3=sQuery(id+"F2.wireOp",EDGE,"E84.trimOffspring");Q4=makeQuery(id+"F2.imprint","IMPRINT",FACE,{"disambiguationData":[TD([[makeQuery(id+"F2.imprint","IMPRINT",EDGE,{"derivedFrom":subQ3}),1.0]])]});}
            var Q5;
            {var subQ3=sQuery(id+"F2.wireOp",EDGE,"E86.trimOffspring");Q5=makeQuery(id+"F2.imprint","IMPRINT",FACE,{"disambiguationData":[TD([[makeQuery(id+"F2.imprint","IMPRINT",EDGE,{"derivedFrom":subQ3}),-1.0]])]});}
            extrude(context, id + "F15", {"entities" : qUnion([Q0, Q1, Q2, Q3, Q4, Q5]), "depth" : 25.4 * mm});
        }
        {
            var Q0;
            Q0=makeQuery(id+"F2.imprint","IMPRINT",FACE,{"disambiguationData":[TD([[makeQuery(id+"F2.imprint","IMPRINT",EDGE,{"derivedFrom":sQuery(id+"F2.wireOp",EDGE,"E74")}),1.0]])]});
            var Q1;
            Q1=makeQuery(id+"F2.imprint","IMPRINT",FACE,{"disambiguationData":[TD([[makeQuery(id+"F2.imprint","IMPRINT",EDGE,{"derivedFrom":sQuery(id+"F2.wireOp",EDGE,"E57")}),1.0]])]});
            var Q2;
            {var subQ3=sQuery(id+"F2.wireOp",EDGE,"E61");Q2=makeQuery(id+"F2.imprint","IMPRINT",FACE,{"disambiguationData":[TD([[makeQuery(id+"F2.imprint","IMPRINT",EDGE,{"derivedFrom":subQ3}),1.0]])]});}
            var Q3;
            Q3=makeQuery(id+"F2.imprint","IMPRINT",FACE,{"disambiguationData":[TD([[makeQuery(id+"F2.imprint","IMPRINT",EDGE,{"derivedFrom":sQuery(id+"F2.wireOp",EDGE,"E97")}),1.0]])]});
            var Q4;
            {var subQ1=sQuery(id+"F2.wireOp",EDGE,"E38");Q4=makeQuery(id+"F2.imprint","IMPRINT",FACE,{"disambiguationData":[TD([[makeQuery(id+"F2.imprint","IMPRINT",EDGE,{"derivedFrom":subQ1}),-1.0]])]});}
            var Q5;
            {var subQ11=sQuery(id+"F2.wireOp",EDGE,"E110");Q5=makeQuery(id+"F2.imprint","IMPRINT",FACE,{"disambiguationData":[TD([[makeQuery(id+"F2.imprint","IMPRINT",EDGE,{"derivedFrom":subQ11}),-1.0]])]});}
            var Q6;
            Q6=makeQuery(id+"F2.imprint","IMPRINT",FACE,{"disambiguationData":[TD([[makeQuery(id+"F2.imprint","IMPRINT",EDGE,{"derivedFrom":sQuery(id+"F2.wireOp",EDGE,"E121")}),1.0]])]});
            var Q7;
            {var subQ2=sQuery(id+"F2.wireOp",EDGE,"E56");Q7=makeQuery(id+"F2.imprint","IMPRINT",FACE,{"disambiguationData":[TD([[makeQuery(id+"F2.imprint","IMPRINT",EDGE,{"derivedFrom":subQ2}),1.0]])]});}
            var Q8;
            {var subQ2=sQuery(id+"F2.wireOp",EDGE,"E56");Q8=makeQuery(id+"F2.imprint","IMPRINT",FACE,{"disambiguationData":[TD([[makeQuery(id+"F2.imprint","IMPRINT",EDGE,{"derivedFrom":subQ2}),1.0]])]});}
            var Q9;
            {var subQ3=sQuery(id+"F2.wireOp",EDGE,"E61");Q9=makeQuery(id+"F2.imprint","IMPRINT",FACE,{"disambiguationData":[TD([[makeQuery(id+"F2.imprint","IMPRINT",EDGE,{"derivedFrom":subQ3}),1.0]])]});}
            var Q10;
            Q10=makeQuery(id+"F2.imprint","IMPRINT",FACE,{"disambiguationData":[TD([[makeQuery(id+"F2.imprint","IMPRINT",EDGE,{"derivedFrom":sQuery(id+"F2.wireOp",EDGE,"E97")}),1.0]])]});
            var Q11;
            {var subQ1=sQuery(id+"F2.wireOp",EDGE,"E38");Q11=makeQuery(id+"F2.imprint","IMPRINT",FACE,{"disambiguationData":[TD([[makeQuery(id+"F2.imprint","IMPRINT",EDGE,{"derivedFrom":subQ1}),-1.0]])]});}
            var Q12;
            {var subQ11=sQuery(id+"F2.wireOp",EDGE,"E110");Q12=makeQuery(id+"F2.imprint","IMPRINT",FACE,{"disambiguationData":[TD([[makeQuery(id+"F2.imprint","IMPRINT",EDGE,{"derivedFrom":subQ11}),-1.0]])]});}
            var Q13;
            Q13=makeQuery(id+"F2.imprint","IMPRINT",FACE,{"disambiguationData":[TD([[makeQuery(id+"F2.imprint","IMPRINT",EDGE,{"derivedFrom":sQuery(id+"F2.wireOp",EDGE,"E121")}),1.0]])]});
            var Q14;
            Q14=makeQuery(id+"F2.imprint","IMPRINT",FACE,{"disambiguationData":[TD([[makeQuery(id+"F2.imprint","IMPRINT",EDGE,{"derivedFrom":sQuery(id+"F2.wireOp",EDGE,"E32.bottom")}),-1.0]])]});
            var Q15;
            {var subQ5=sQuery(id+"F2.wireOp",EDGE,"E143");Q15=makeQuery(id+"F2.imprint","IMPRINT",FACE,{"disambiguationData":[TD([[makeQuery(id+"F2.imprint","IMPRINT",EDGE,{"derivedFrom":subQ5}),1.0]])]});}
            var Q16;
            Q16=makeQuery(id+"F2.imprint","IMPRINT",FACE,{"disambiguationData":[TD([[makeQuery(id+"F2.imprint","IMPRINT",EDGE,{"derivedFrom":sQuery(id+"F2.wireOp",EDGE,"E31.bottom")}),-1.0]])]});
            var Q17;
            {var subQ10=sQuery(id+"F2.wireOp",EDGE,"E45");Q17=makeQuery(id+"F2.imprint","IMPRINT",FACE,{"disambiguationData":[TD([[makeQuery(id+"F2.imprint","IMPRINT",EDGE,{"derivedFrom":subQ10}),-1.0]])]});}
            var Q18;
            {var subQ0=sQuery(id+"F2.wireOp",EDGE,"E158");Q18=makeQuery(id+"F2.imprint","IMPRINT",FACE,{"disambiguationData":[TD([[makeQuery(id+"F2.imprint","IMPRINT",EDGE,{"derivedFrom":subQ0}),-1.0]])]});}
            var Q19;
            {var subQ5=sQuery(id+"F2.wireOp",EDGE,"E146");Q19=makeQuery(id+"F2.imprint","IMPRINT",FACE,{"disambiguationData":[TD([[makeQuery(id+"F2.imprint","IMPRINT",EDGE,{"derivedFrom":subQ5}),1.0]])]});}
            var Q20;
            {var subQ5=sQuery(id+"F2.wireOp",EDGE,"E144");Q20=makeQuery(id+"F2.imprint","IMPRINT",FACE,{"disambiguationData":[TD([[makeQuery(id+"F2.imprint","IMPRINT",EDGE,{"derivedFrom":subQ5}),1.0]])]});}
            var Q21;
            {var subQ0=sQuery(id+"F2.wireOp",EDGE,"E134");Q21=makeQuery(id+"F2.imprint","IMPRINT",FACE,{"disambiguationData":[TD([[makeQuery(id+"F2.imprint","IMPRINT",EDGE,{"derivedFrom":subQ0}),1.0]])]});}
            var Q22;
            {var subQ5=sQuery(id+"F2.wireOp",EDGE,"E134");Q22=makeQuery(id+"F2.imprint","IMPRINT",FACE,{"disambiguationData":[TD([[makeQuery(id+"F2.imprint","IMPRINT",EDGE,{"derivedFrom":subQ5}),-1.0]])]});}
            var Q23;
            {var subQ0=sQuery(id+"F2.wireOp",EDGE,"E141");Q23=makeQuery(id+"F2.imprint","IMPRINT",FACE,{"disambiguationData":[TD([[makeQuery(id+"F2.imprint","IMPRINT",EDGE,{"derivedFrom":subQ0}),1.0]])]});}
            extrude(context, id + "F16", {"entities" : qUnion([Q0, Q1, Q2, Q3, Q4, Q5, Q6, Q7, Q8, Q9, Q10, Q11, Q12, Q13, Q14, Q15, Q16, Q17, Q18, Q19, Q20, Q21, Q22, Q23]), "depth" : 25.4 * mm});
        }
        {
            var Q0;
            Q0=makeQuery(id+"F2.imprint","IMPRINT",FACE,{"disambiguationData":[TD([[makeQuery(id+"F2.imprint","IMPRINT",EDGE,{"derivedFrom":sQuery(id+"F2.wireOp",EDGE,"E102.bottom")}),-1.0]])]});
            var Q1;
            Q1=makeQuery(id+"F2.imprint","IMPRINT",FACE,{"disambiguationData":[TD([[makeQuery(id+"F2.imprint","IMPRINT",EDGE,{"derivedFrom":sQuery(id+"F2.wireOp",EDGE,"E135")}),-1.0]])]});
            var Q2;
            {var subQ0=sQuery(id+"F2.wireOp",EDGE,"E55");var subQ4=makeQuery(id+"F2.imprint","IMPRINT",VERTEX,{"derivedFrom":subQ0});Q2=makeQuery(id+"F2.imprint","IMPRINT",FACE,{"disambiguationData":[TD([[makeQuery(id+"F2.imprint","IMPRINT",EDGE,{"disambiguationData":[TD([[subQ4,1.0]])],"derivedFrom":subQ0}),-1.0]])]});}
            var Q3;
            {var subQ0=sQuery(id+"F2.wireOp",EDGE,"E55");var subQ4=makeQuery(id+"F2.imprint","IMPRINT",VERTEX,{"derivedFrom":subQ0});Q3=makeQuery(id+"F2.imprint","IMPRINT",FACE,{"disambiguationData":[TD([[makeQuery(id+"F2.imprint","IMPRINT",EDGE,{"disambiguationData":[TD([[subQ4,1.0]])],"derivedFrom":subQ0}),1.0]])]});}
            var Q4;
            Q4=makeQuery(id+"F2.imprint","IMPRINT",FACE,{"disambiguationData":[TD([[makeQuery(id+"F2.imprint","IMPRINT",EDGE,{"derivedFrom":sQuery(id+"F2.wireOp",EDGE,"E51.bottom")}),1.0]])]});
            var Q5;
            {var subQ0=sQuery(id+"F2.wireOp",EDGE,"E51.top");var subQ1=makeQuery(id+"F2.imprint","INTERSECT",VERTEX,{"derivedFrom":[subQ0,sQuery(id+"F2.wireOp",EDGE,"E55")]});Q5=makeQuery(id+"F2.imprint","IMPRINT",FACE,{"disambiguationData":[TD([[makeQuery(id+"F2.imprint","IMPRINT",EDGE,{"disambiguationData":[TD([[subQ1,1.0]])],"derivedFrom":subQ0}),-1.0]])]});}
            var Q6;
            Q6=makeQuery(id+"F2.imprint","IMPRINT",FACE,{"disambiguationData":[TD([[makeQuery(id+"F2.imprint","IMPRINT",EDGE,{"derivedFrom":sQuery(id+"F2.wireOp",EDGE,"E172")}),1.0]])]});
            extrude(context, id + "F17", {"entities" : qUnion([Q0, Q1, Q2, Q3, Q4, Q5, Q6]), "depth" : 25.4 * mm});
        }
        {
            var Q0;
            Q0=makeQuery(id+"F2.imprint","IMPRINT",FACE,{"disambiguationData":[TD([[makeQuery(id+"F2.imprint","IMPRINT",EDGE,{"derivedFrom":sQuery(id+"F2.wireOp",EDGE,"E160")}),1.0]])]});
            var Q1;
            {var subQ1=sQuery(id+"F2.wireOp",EDGE,"E32.right");Q1=makeQuery(id+"F2.imprint","IMPRINT",FACE,{"disambiguationData":[TD([[makeQuery(id+"F2.imprint","IMPRINT",EDGE,{"derivedFrom":subQ1}),1.0]])]});}
            var Q2;
            {var subQ0=sQuery(id+"F2.wireOp",EDGE,"E32.top");Q2=makeQuery(id+"F2.imprint","IMPRINT",FACE,{"disambiguationData":[TD([[makeQuery(id+"F2.imprint","IMPRINT",EDGE,{"derivedFrom":subQ0}),-1.0]])]});}
            var Q3;
            {var subQ1=sQuery(id+"F2.wireOp",EDGE,"E32.top");Q3=makeQuery(id+"F2.imprint","IMPRINT",FACE,{"disambiguationData":[TD([[makeQuery(id+"F2.imprint","IMPRINT",EDGE,{"derivedFrom":subQ1}),1.0]])]});}
            extrude(context, id + "F18", {"entities" : qUnion([Q0, Q1, Q2, Q3]), "depth" : 25.4 * mm});
        }
        {
            var Q0;
            {var subQ54=sQuery(id+"F2.wireOp",EDGE,"E0.bottom");Q0=makeQuery(id+"F2.imprint","IMPRINT",FACE,{"disambiguationData":[TD([[makeQuery(id+"F2.imprint","IMPRINT",EDGE,{"derivedFrom":subQ54}),1.0]])]});}
            var Q1;
            {var subQ1=sQuery(id+"F2.wireOp",EDGE,"E39");Q1=makeQuery(id+"F2.imprint","IMPRINT",FACE,{"disambiguationData":[TD([[makeQuery(id+"F2.imprint","IMPRINT",EDGE,{"derivedFrom":subQ1}),-1.0]])]});}
            extrude(context, id + "F19", {"entities" : qUnion([Q0, Q1]), "depth" : 6.35 * mm});
        }
    });
